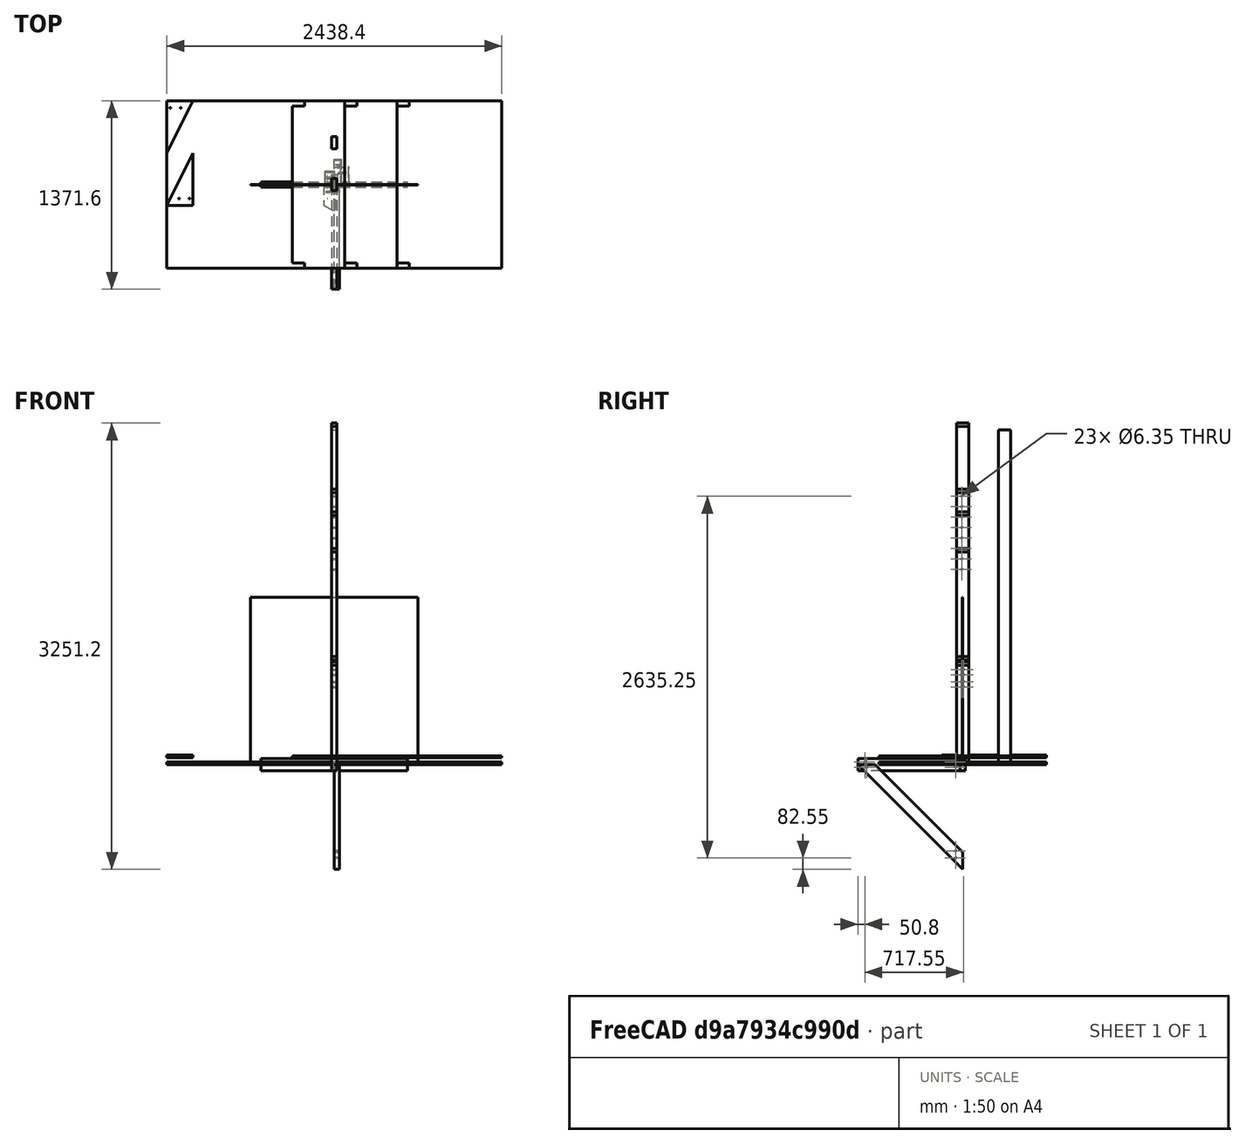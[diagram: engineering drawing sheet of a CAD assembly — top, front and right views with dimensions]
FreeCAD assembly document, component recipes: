
FREECAD ASSEMBLY — COMPONENT RECIPES ("workshop")

This assembly document has 20 components, labeled P0..P19 below (a component is one placed body or linked part). 20 of them carry a construction recipe — the FreeCAD feature program that regenerates the part from scratch, quoted from this document or its linked companion documents; the rest are supplied as boundary geometry only. No exploded tour is included for this assembly.
COMPONENT P0 — recipe-attached ("P_Electronics_CableMount", modeled in this document).
Construction recipe (the document's own serialized feature program — sketch geometry with constraints, then the solid features built on it; lengths are millimeters unless a unit is written):

FEATURE [Sketcher::SketchObject] Sketch  label="S_Electronics_CableMount_Body"
  FullyConstrained = true
  MapMode = 5
  Support = -> [XY_Plane001]
  sketch-geometry (8):
    g0: LineSegment StartX=12.5 StartY=42.5 StartZ=0 EndX=12.5 EndY=12.5 EndZ=0
    g1: LineSegment StartX=-12.5 StartY=12.5 StartZ=0 EndX=-12.5 EndY=42.5 EndZ=0
    g2: ArcOfCircle CenterX=3e-15 CenterY=12.5 CenterZ=0 NormalX=0 NormalY=0 NormalZ=1 AngleXU=0 Radius=12.5 StartAngle=3.14159 EndAngle=6.28319
    g3: LineSegment StartX=22.5 StartY=42.5 StartZ=0 EndX=22.5 EndY=12.5 EndZ=0
    g4: LineSegment StartX=-22.5 StartY=12.5 StartZ=0 EndX=-22.5 EndY=42.5 EndZ=0
    g5: ArcOfCircle CenterX=5.7957e-12 CenterY=12.5 CenterZ=0 NormalX=0 NormalY=0 NormalZ=1 AngleXU=0 Radius=22.5 StartAngle=3.14159 EndAngle=6.28319
    g6: LineSegment StartX=-12.5 StartY=42.5 StartZ=0 EndX=-22.5 EndY=42.5 EndZ=0
    g7: LineSegment StartX=22.5 StartY=42.5 StartZ=0 EndX=12.5 EndY=42.5 EndZ=0
  constraints (20):
    c: Vertical(g0)
    c: Symmetric(g0,g1,g-2)
    c: PointOnObject(g-1,g2)
    c: Tangent(g2,g0) = 1.5708
    c: Tangent(g1,g2) = 1.5708
    c: Vertical(g3)
    c: Coincident(g6,g1)
    c: Coincident(g6,g4)
    c: Coincident(g7,g3)
    c: Coincident(g7,g0)
    c: Tangent(g5,g3) = 1.5708
    c: Tangent(g4,g5) = 1.5708
    c: Horizontal(g6)
    c: Horizontal(g7)
    c: Horizontal(g4,g3)
    c: Horizontal(g4,g1)
    c: Symmetric(g3,g4,g-2)
    c: DistanceX(g7,g7) = 10
    c: DistanceX(g1,g0) = 25
    c: DistanceY(g3,g3) = 30
FEATURE [PartDesign::Pad] Pad  label="PAD_Electronics_CableMount"
  Direction = (0,0,1)
  Length = 10
  Length2 = 10
  Profile = -> Sketch
  ReferenceAxis = -> Sketch [N_Axis]
  Type = 0
FEATURE [Sketcher::SketchObject] Sketch001  label="S_Electronics_CableMount_Hole"
  AttachmentOffset = pos=(0,0,30) rot=(0,0,1;0rad)
  FullyConstrained = true
  MapMode = 5
  Placement = pos=(30,-6.7e-15,6.7e-15) rot=(0.57735,0.57735,0.57735;2.0944rad)
  Support = -> [YZ_Plane001]
  sketch-geometry (1):
    g0: Circle CenterX=35 CenterY=5 CenterZ=0 NormalX=0 NormalY=0 NormalZ=1 AngleXU=0 Radius=2.5
  constraints (3):
    c: Diameter(g0) = 5
    c: DistanceY(g-1,g0) = 5
    c: DistanceX(g-1,g0) = 35
FEATURE [PartDesign::Hole] Hole  label="HOLE_Electronics_CableMount"
  BaseFeature = -> Pad
  CustomThreadClearance = 0
  Depth = 161.858
  DepthType = 1
  Diameter = 5.5
  DrillForDepth = false
  DrillPoint = 0
  DrillPointAngle = 118
  HoleCutCountersinkAngle = 90
  HoleCutCustomValues = false
  HoleCutDepth = 0
  HoleCutDiameter = 6.1
  HoleCutType = 0
  ModelThread = false
  Profile = -> Sketch001
  Tapered = false
  TaperedAngle = 90
  ThreadClass = 0
  ThreadDepth = 161.858
  ThreadDepthType = 0
  ThreadDirection = 0
  ThreadFit = 0
  ThreadSize = 13
  ThreadType = 1
  Threaded = false
  UseCustomThreadClearance = false
FEATURE [PartDesign::Body] Body  label="B_Electronics_CableMount"
  Group = -> [Sketch,Pad,Sketch001,Hole]
  Origin = -> Origin001
  Tip = -> Hole
COMPONENT P1 — recipe-attached ("P_Electronics_CableMountSpacer", modeled in this document).
Construction recipe (the document's own serialized feature program — sketch geometry with constraints, then the solid features built on it; lengths are millimeters unless a unit is written):

FEATURE [Sketcher::SketchObject] Sketch002  label="S_Electronics_CableMountSpacer"
  FullyConstrained = true
  MapMode = 5
  Support = -> [XY_Plane003]
  sketch-geometry (7):
    g0: LineSegment StartX=-25 StartY=0 StartZ=0 EndX=25 EndY=0 EndZ=0
    g1: LineSegment StartX=25 StartY=0 StartZ=0 EndX=25 EndY=70 EndZ=0
    g2: LineSegment StartX=25 StartY=70 StartZ=0 EndX=-25 EndY=70 EndZ=0
    g3: LineSegment StartX=-25 StartY=70 StartZ=0 EndX=-25 EndY=0 EndZ=0
    g4: Circle CenterX=0 CenterY=60 CenterZ=0 NormalX=0 NormalY=0 NormalZ=1 AngleXU=0 Radius=2.5
    g5: Circle CenterX=0 CenterY=35 CenterZ=0 NormalX=0 NormalY=0 NormalZ=1 AngleXU=0 Radius=2.5
    g6: Circle CenterX=0 CenterY=10 CenterZ=0 NormalX=0 NormalY=0 NormalZ=1 AngleXU=0 Radius=2.5
  constraints (20):
    c: Coincident(g0,g1)
    c: Coincident(g1,g2)
    c: Coincident(g2,g3)
    c: Coincident(g3,g0)
    c: Horizontal(g2)
    c: Vertical(g1)
    c: Vertical(g3)
    c: PointOnObject(g0,g-1)
    c: Symmetric(g0,g0,g-2)
    c: DistanceX(g2,g2) = 50
    c: DistanceY(g1,g1) = 70
    c: PointOnObject(g4,g-2)
    c: PointOnObject(g5,g-2)
    c: PointOnObject(g6,g-2)
    c: Equal(g6,g5)
    c: Equal(g5,g4)
    c: Diameter(g4) = 5
    c: DistanceY(g-1,g6) = 10
    c: DistanceY(g4,g2) = 10
    c: DistanceY(g-1,g5) = 35
FEATURE [PartDesign::Pad] Pad001  label="PAD_Electronics_CableMountSpacer"
  Direction = (0,0,1)
  Length = 2
  Length2 = 10
  Profile = -> Sketch002
  ReferenceAxis = -> Sketch002 [N_Axis]
  Type = 0
FEATURE [Sketcher::SketchObject] Sketch003  label="S_Electronics_CableMountSpacer_Side"
  FullyConstrained = true
  MapMode = 5
  Support = -> [XY_Plane003]
  expr: Constraints[9] = 41.5 mm / 2
  sketch-geometry (4):
    g0: LineSegment StartX=20.75 StartY=70 StartZ=0 EndX=25 EndY=70 EndZ=0
    g1: LineSegment StartX=25 StartY=70 StartZ=0 EndX=25 EndY=0 EndZ=0
    g2: LineSegment StartX=25 StartY=0 StartZ=0 EndX=20.75 EndY=0 EndZ=0
    g3: LineSegment StartX=20.75 StartY=0 StartZ=0 EndX=20.75 EndY=70 EndZ=0
  constraints (12):
    c: Coincident(g0,g1)
    c: Coincident(g1,g2)
    c: Coincident(g2,g3)
    c: Coincident(g3,g0)
    c: Horizontal(g0)
    c: Horizontal(g2)
    c: Vertical(g1)
    c: Vertical(g3)
    c: PointOnObject(g1,g-1)
    c: DistanceX(g-1,g2) = 20.75
    c: DistanceX(g-1,g1) = 25
    c: DistanceY(g1,g1) = 70
FEATURE [PartDesign::Pad] Pad002  label="PAD_Electronics_CableMountSpacer_Side"
  BaseFeature = -> Pad001
  Direction = (0,0,1)
  Length = 4
  Length2 = 10
  Profile = -> Sketch003
  ReferenceAxis = -> Sketch003 [N_Axis]
  Type = 0
FEATURE [PartDesign::Mirrored] Mirrored  label="PAT_Electronics_CableMountSpacer_Side"
  BaseFeature = -> Pad002
  MirrorPlane = -> Sketch003 [V_Axis]
  Originals = -> [Pad002]
FEATURE [PartDesign::Body] Body001  label="B_Electronics_CableMountSpacer"
  Group = -> [Sketch002,Pad001,Sketch003,Pad002,Mirrored]
  Origin = -> Origin003
  Tip = -> Mirrored
COMPONENT P2 — recipe-attached ("P_Workbench_Top", modeled in this document).
Construction recipe (the document's own serialized feature program — sketch geometry with constraints, then the solid features built on it; lengths are millimeters unless a unit is written):

FEATURE [Sketcher::SketchObject] Sketch005  label="S_Workbench_Top_Base"
  FullyConstrained = true
  MapMode = 5
  Support = -> [XY_Plane007]
  expr: Constraints[8] = <<S_Workbench_Master>>.Constraints.TableWidth
  sketch-geometry (4):
    g0: LineSegment StartX=-609.6 StartY=0 StartZ=0 EndX=609.6 EndY=0 EndZ=0
    g1: LineSegment StartX=609.6 StartY=0 StartZ=0 EndX=609.6 EndY=-762 EndZ=0
    g2: LineSegment StartX=609.6 StartY=-762 StartZ=0 EndX=-609.6 EndY=-762 EndZ=0
    g3: LineSegment StartX=-609.6 StartY=-762 StartZ=0 EndX=-609.6 EndY=0 EndZ=0
  constraints (11):
    c: Coincident(g0,g1)
    c: Coincident(g1,g2)
    c: Coincident(g2,g3)
    c: Coincident(g3,g0)
    c: Horizontal(g0)
    c: Horizontal(g2)
    c: Vertical(g1)
    c: Vertical(g3)
    c: DistanceX(g0,g0) = 1219.2
    c: DistanceY(g1,g1) = 762
    c: Symmetric(g0,g0,g-1)
FEATURE [PartDesign::Pad] Pad004  label="PAD_Workbench_Top_Base"
  Direction = (0,0,1)
  Length = 12.7
  Length2 = 10
  Profile = -> Sketch005
  ReferenceAxis = -> Sketch005 [N_Axis]
  Type = 0
  expr: Length = <<S_Workbench_Master>>.Constraints.TableThickness
FEATURE [Sketcher::SketchObject] Sketch006  label="S_Workbench_Top_BackHole"
  ExternalGeometry = -> [Pad004]
  FullyConstrained = true
  MapMode = 5
  Placement = pos=(0,0,12.7) rot=(0,0,1;0rad)
  Support = -> [Pad004]
  expr: Constraints[8] = Sketch009.Constraints.TwobyfourWidth
  expr: Constraints[9] = Sketch009.Constraints.TwobyfourHeight
  sketch-geometry (4):
    g0: LineSegment StartX=-571.5 StartY=0 StartZ=0 EndX=-609.6 EndY=0 EndZ=0
    g1: LineSegment StartX=-609.6 StartY=0 StartZ=0 EndX=-609.6 EndY=-88.9 EndZ=0
    g2: LineSegment StartX=-609.6 StartY=-88.9 StartZ=0 EndX=-571.5 EndY=-88.9 EndZ=0
    g3: LineSegment StartX=-571.5 StartY=-88.9 StartZ=0 EndX=-571.5 EndY=0 EndZ=0
  constraints (11):
    c: Coincident(g0,g1)
    c: Coincident(g1,g2)
    c: Coincident(g2,g3)
    c: Coincident(g3,g0)
    c: Horizontal(g0)
    c: Horizontal(g2)
    c: Vertical(g1)
    c: Vertical(g3)
    c: DistanceX(g0,g0) = 38.1
    c: DistanceY(g3,g3) = 88.9
    c: Coincident(g0,g-3)
FEATURE [PartDesign::Pocket] Pocket  label="POCKET_Workbench_Top_BackHole"
  BaseFeature = -> Pad004
  Direction = (0,0,-1)
  Length = 25.4
  Length2 = 5
  Profile = -> Sketch006
  ReferenceAxis = -> Sketch006 [N_Axis]
  Type = 0
FEATURE [PartDesign::Mirrored] Mirrored001  label="PAT_B_Workbench_Top_BackHoles"
  BaseFeature = -> Pocket
  MirrorPlane = -> Sketch006 [V_Axis]
  Originals = -> [Pocket]
FEATURE [PartDesign::Body] Body003  label="B_Workbench_Top"
  Group = -> [Sketch005,Pad004,Sketch006,Pocket,Mirrored001]
  Origin = -> Origin007
  Tip = -> Mirrored001
COMPONENT P3 — recipe-attached ("P_Workbench_BackLeg", modeled in this document).
Construction recipe (the document's own serialized feature program — sketch geometry with constraints, then the solid features built on it; lengths are millimeters unless a unit is written):

FEATURE [Sketcher::SketchObject] Sketch007  label="S_Workbench_BackLeg_Base"
  FullyConstrained = true
  MapMode = 5
  Support = -> [XY_Plane010]
  expr: Constraints[10] = Sketch009.Constraints.TwobyfourHeight
  expr: Constraints[9] = Sketch009.Constraints.TwobyfourWidth
  sketch-geometry (4):
    g0: LineSegment StartX=-19.05 StartY=44.45 StartZ=0 EndX=19.05 EndY=44.45 EndZ=0
    g1: LineSegment StartX=19.05 StartY=44.45 StartZ=0 EndX=19.05 EndY=-44.45 EndZ=0
    g2: LineSegment StartX=19.05 StartY=-44.45 StartZ=0 EndX=-19.05 EndY=-44.45 EndZ=0
    g3: LineSegment StartX=-19.05 StartY=-44.45 StartZ=0 EndX=-19.05 EndY=44.45 EndZ=0
  constraints (11):
    c: Coincident(g0,g1)
    c: Coincident(g1,g2)
    c: Coincident(g2,g3)
    c: Coincident(g3,g0)
    c: Horizontal(g0)
    c: Horizontal(g2)
    c: Vertical(g1)
    c: Vertical(g3)
    c: Symmetric(g0,g1,g-1)
    c: DistanceX(g0,g0) = 38.1
    c: DistanceY(g1,g1) = 88.9
FEATURE [PartDesign::Pad] Pad005  label="PAD_Workbench_BackLeg"
  Direction = (0,0,1)
  Length = 1981.2
  Length2 = 10
  Profile = -> Sketch007
  ReferenceAxis = -> Sketch007 [N_Axis]
  Type = 0
  expr: Length = <<S_Workbench_Master>>.Constraints.BackLegHeight
FEATURE [Sketcher::SketchObject] Sketch019  label="S_Workbench_BackLeg_Holes"
  FullyConstrained = true
  MapMode = 5
  Placement = pos=(0,0,0) rot=(0.57735,0.57735,0.57735;2.0944rad)
  Support = -> [YZ_Plane010]
  expr: Constraints[15] = <<S_Workbench_Master>>.Constraints.ShelfHeight - 1 in
  expr: Constraints[16] = <<S_Workbench_Master>>.Constraints.ShelfHeight + <<S_Workbench_Master>>.Constraints.ShelfSpacing - 1 in
  expr: Constraints[22] = Sketch009.Constraints.TwobyfourHeight - 2 in
  expr: Constraints[23] = Sketch009.Constraints.TwobyfourHeight
  expr: Constraints[25] = <<S_Workbench_Master>>.Constraints.BackLegHeight
  expr: Constraints[2] = Sketch009.Constraints.BoltDiameter
  expr: Constraints[3] = <<S_Workbench_Master>>.Constraints.TableHeight - 1.75 in
  expr: Constraints[4] = Sketch009.Constraints.TwobyfourHeight - 2 in
  sketch-geometry (13):
    g0: Circle CenterX=-6.35 CenterY=692.15 CenterZ=0 NormalX=0 NormalY=0 NormalZ=1 AngleXU=0 Radius=3.175
    g1: Circle CenterX=-6.35 CenterY=654.05 CenterZ=0 NormalX=0 NormalY=0 NormalZ=1 AngleXU=0 Radius=3.175
    g2: Circle CenterX=-6.35 CenterY=1498.6 CenterZ=0 NormalX=0 NormalY=0 NormalZ=1 AngleXU=0 Radius=3.175
    g3: Circle CenterX=-6.35 CenterY=1422.4 CenterZ=0 NormalX=0 NormalY=0 NormalZ=1 AngleXU=0 Radius=3.175
    g4: Circle CenterX=-6.35 CenterY=1803.4 CenterZ=0 NormalX=0 NormalY=0 NormalZ=1 AngleXU=0 Radius=3.175
    g5: Circle CenterX=-6.35 CenterY=1727.2 CenterZ=0 NormalX=0 NormalY=0 NormalZ=1 AngleXU=0 Radius=3.175
    g6: Circle CenterX=-6.35 CenterY=603.25 CenterZ=0 NormalX=0 NormalY=0 NormalZ=1 AngleXU=0 Radius=3.175
    g7: Circle CenterX=-6.35 CenterY=565.15 CenterZ=0 NormalX=0 NormalY=0 NormalZ=1 AngleXU=0 Radius=3.175
    g8: GeomPoint X=0 Y=1981.2 Z=0
    g9: Circle CenterX=-6.35 CenterY=1879.6 CenterZ=0 NormalX=0 NormalY=0 NormalZ=1 AngleXU=0 Radius=3.175
    g10: Circle CenterX=-6.35 CenterY=1955.8 CenterZ=0 NormalX=0 NormalY=0 NormalZ=1 AngleXU=0 Radius=3.175
    g11: Circle CenterX=-6.35 CenterY=1651 CenterZ=0 NormalX=0 NormalY=0 NormalZ=1 AngleXU=0 Radius=3.175
    g12: Circle CenterX=-6.35 CenterY=1574.8 CenterZ=0 NormalX=0 NormalY=0 NormalZ=1 AngleXU=0 Radius=3.175
  constraints (41):
    c: Vertical(g1,g0)
    c: Equal(g0,g1)
    c: Diameter(g0) = 6.35
    c: DistanceY(g-1,g0) = 692.15
    c: DistanceY(g1,g0) = 38.1
    c: DistanceX(g0,g-1) = 6.35
    c: Vertical(g4,g5)
    c: Vertical(g5,g2)
    c: Vertical(g2,g3)
    c: Equal(g4,g5)
    c: Equal(g5,g2)
    c: Equal(g2,g3)
    c: Equal(g3,g0)
    c: DistanceY(g3,g2) = 76.2
    c: DistanceY(g5,g4) = 76.2
    c: DistanceY(g-1,g2) = 1498.6
    c: DistanceY(g-1,g4) = 1803.4
    c: Vertical(g0,g3)
    c: Equal(g7,g6)
    c: Vertical(g6,g7)
    c: Vertical(g7,g1)
    c: Equal(g7,g1)
    c: DistanceY(g7,g6) = 38.1
    c: DistanceY(g6,g0) = 88.9
    c: PointOnObject(g8,g-2)
    c: DistanceY(g-1,g8) = 1981.2
    c: DistanceY(g4,g8) = 177.8
    c: Vertical(g9,g10)
    c: Vertical(g10,g4)
    c: Equal(g9,g10)
    c: Equal(g10,g4)
    c: DistanceY(g4,g9) = 76.2
    c: DistanceY(g9,g10) = 76.2
    c: DistanceY(g10,g8) = 25.4
    c: Equal(g11,g12)
    c: Vertical(g5,g11)
    c: Vertical(g11,g12)
    c: DistanceY(g11,g5) = 76.2
    c: DistanceY(g12,g11) = 76.2
    c: DistanceY(g2,g12) = 76.2
    c: Equal(g11,g5)
FEATURE [PartDesign::Pocket] Pocket004  label="POCKET_Workbench_BackLeg_Holes"
  BaseFeature = -> Pad005
  Direction = (-1,2e-16,-3e-16)
  Length = 76.2
  Length2 = 5
  Midplane = true
  Profile = -> Sketch019
  ReferenceAxis = -> Sketch019 [N_Axis]
  Type = 0
  expr: Length = Sketch009.Constraints.TwobyfourWidth * 2
FEATURE [PartDesign::Body] Body004  label="B_Workbench_BackLeg"
  Group = -> [Sketch007,Pad005,Sketch019,Pocket004]
  Origin = -> Origin010
  Tip = -> Pocket004
COMPONENT P4 — recipe-attached ("P_Workbench_FrontLeg", modeled in this document).
Construction recipe (the document's own serialized feature program — sketch geometry with constraints, then the solid features built on it; lengths are millimeters unless a unit is written):

FEATURE [Sketcher::SketchObject] Sketch008  label="S_Workbench_FrontLeg_Base"
  FullyConstrained = true
  MapMode = 5
  Support = -> [XY_Plane012]
  expr: Constraints[10] = Sketch009.Constraints.TwobyfourHeight
  expr: Constraints[9] = Sketch009.Constraints.TwobyfourWidth
  sketch-geometry (4):
    g0: LineSegment StartX=-19.05 StartY=44.45 StartZ=0 EndX=19.05 EndY=44.45 EndZ=0
    g1: LineSegment StartX=19.05 StartY=44.45 StartZ=0 EndX=19.05 EndY=-44.45 EndZ=0
    g2: LineSegment StartX=19.05 StartY=-44.45 StartZ=0 EndX=-19.05 EndY=-44.45 EndZ=0
    g3: LineSegment StartX=-19.05 StartY=-44.45 StartZ=0 EndX=-19.05 EndY=44.45 EndZ=0
  constraints (11):
    c: Coincident(g0,g1)
    c: Coincident(g1,g2)
    c: Coincident(g2,g3)
    c: Coincident(g3,g0)
    c: Horizontal(g0)
    c: Horizontal(g2)
    c: Vertical(g1)
    c: Vertical(g3)
    c: Symmetric(g0,g1,g-1)
    c: DistanceX(g0,g0) = 38.1
    c: DistanceY(g1,g1) = 88.9
FEATURE [PartDesign::Pad] Pad006  label="PAD_Workbench_FrontLeg_Base"
  Direction = (0,0,1)
  Length = 723.9
  Length2 = 10
  Profile = -> Sketch008
  ReferenceAxis = -> Sketch008 [N_Axis]
  Type = 0
  expr: Length = Sketch009.Constraints.FrontLegHeight
FEATURE [Sketcher::SketchObject] Sketch018  label="S_Workbench_FrontLeg_Holes"
  FullyConstrained = true
  MapMode = 5
  Placement = pos=(0,0,0) rot=(0.57735,0.57735,0.57735;2.0944rad)
  Support = -> [YZ_Plane012]
  expr: Constraints[10] = Sketch009.Constraints.TwobyfourHeight - 2 in
  expr: Constraints[11] = Sketch009.Constraints.TwobyfourHeight
  expr: Constraints[1] = Sketch009.Constraints.BoltDiameter
  expr: Constraints[2] = Sketch009.Constraints.TwobyfourHeight - 2 in
  expr: Constraints[4] = <<S_Workbench_Master>>.Constraints.TableHeight - 1.75 in
  sketch-geometry (4):
    g0: Circle CenterX=6.35 CenterY=692.15 CenterZ=0 NormalX=0 NormalY=0 NormalZ=1 AngleXU=0 Radius=3.175
    g1: Circle CenterX=6.35 CenterY=654.05 CenterZ=0 NormalX=0 NormalY=0 NormalZ=1 AngleXU=0 Radius=3.175
    g2: Circle CenterX=6.35 CenterY=603.25 CenterZ=0 NormalX=0 NormalY=0 NormalZ=1 AngleXU=0 Radius=3.175
    g3: Circle CenterX=6.35 CenterY=565.15 CenterZ=0 NormalX=0 NormalY=0 NormalZ=1 AngleXU=0 Radius=3.175
  constraints (12):
    c: Equal(g0,g1)
    c: Diameter(g1) = 6.35
    c: DistanceY(g1,g0) = 38.1
    c: Vertical(g0,g1)
    c: DistanceY(g-1,g0) = 692.15
    c: DistanceX(g-1,g1) = 6.35
    c: Equal(g2,g1)
    c: Vertical(g3,g2)
    c: Vertical(g2,g1)
    c: Equal(g3,g2)
    c: DistanceY(g3,g2) = 38.1
    c: DistanceY(g2,g0) = 88.9
FEATURE [PartDesign::Pocket] Pocket003  label="POCKET_Workbench_FrontLeg_Holes"
  BaseFeature = -> Pad006
  Direction = (-1,2e-16,-3e-16)
  Length = 76.2
  Length2 = 5
  Midplane = true
  Profile = -> Sketch018
  ReferenceAxis = -> Sketch018 [N_Axis]
  Type = 0
  expr: Length = Sketch009.Constraints.TwobyfourWidth * 2
FEATURE [PartDesign::Body] Body005  label="B_Workbench_FrontLeg"
  Group = -> [Sketch008,Pad006,Sketch018,Pocket003]
  Origin = -> Origin012
  Tip = -> Pocket003
COMPONENT P5 — recipe-attached ("P_Workbench_Shelf", modeled in this document).
Construction recipe (the document's own serialized feature program — sketch geometry with constraints, then the solid features built on it; lengths are millimeters unless a unit is written):

FEATURE [Sketcher::SketchObject] Sketch010  label="S_Workbench_Shelf_Base"
  FullyConstrained = true
  MapMode = 5
  Support = -> [XY_Plane014]
  expr: Constraints[10] = <<S_Workbench_Master>>.Constraints.ShelfDepth
  expr: Constraints[9] = <<S_Workbench_Master>>.Constraints.TableWidth
  sketch-geometry (4):
    g0: LineSegment StartX=-609.6 StartY=0 StartZ=0 EndX=609.6 EndY=0 EndZ=0
    g1: LineSegment StartX=609.6 StartY=0 StartZ=0 EndX=609.6 EndY=-381 EndZ=0
    g2: LineSegment StartX=609.6 StartY=-381 StartZ=0 EndX=-609.6 EndY=-381 EndZ=0
    g3: LineSegment StartX=-609.6 StartY=-381 StartZ=0 EndX=-609.6 EndY=0 EndZ=0
  constraints (11):
    c: Coincident(g0,g1)
    c: Coincident(g1,g2)
    c: Coincident(g2,g3)
    c: Coincident(g3,g0)
    c: Horizontal(g0)
    c: Horizontal(g2)
    c: Vertical(g1)
    c: Vertical(g3)
    c: Symmetric(g0,g0,g-1)
    c: DistanceX(g0,g0) = 1219.2
    c: DistanceY(g1,g1) = 381
FEATURE [PartDesign::Pad] Pad007  label="PAD_Workbench_Shelf_Base"
  Direction = (0,0,1)
  Length = 12.7
  Length2 = 10
  Profile = -> Sketch010
  ReferenceAxis = -> Sketch010 [N_Axis]
  Type = 0
  expr: Length = <<S_Workbench_Master>>.Constraints.TableThickness
FEATURE [Sketcher::SketchObject] Sketch011  label="S_Workbench_Shelf_LegSlot"
  FullyConstrained = true
  MapMode = 5
  Support = -> [XY_Plane014]
  expr: Constraints[10] = Sketch009.Constraints.TwobyfourWidth
  expr: Constraints[11] = <<S_Workbench_Master>>.Constraints.TableWidth / 2
  expr: Constraints[9] = Sketch009.Constraints.TwobyfourHeight
  sketch-geometry (4):
    g0: LineSegment StartX=-609.6 StartY=0 StartZ=0 EndX=-571.5 EndY=0 EndZ=0
    g1: LineSegment StartX=-571.5 StartY=0 StartZ=0 EndX=-571.5 EndY=-88.9 EndZ=0
    g2: LineSegment StartX=-571.5 StartY=-88.9 StartZ=0 EndX=-609.6 EndY=-88.9 EndZ=0
    g3: LineSegment StartX=-609.6 StartY=-88.9 StartZ=0 EndX=-609.6 EndY=0 EndZ=0
  constraints (12):
    c: Coincident(g0,g1)
    c: Coincident(g1,g2)
    c: Coincident(g2,g3)
    c: Coincident(g3,g0)
    c: Horizontal(g0)
    c: Horizontal(g2)
    c: Vertical(g1)
    c: Vertical(g3)
    c: Horizontal(g0,g-1)
    c: DistanceY(g1,g1) = 88.9
    c: DistanceX(g2,g2) = 38.1
    c: DistanceX(g0,g-1) = 609.6
FEATURE [PartDesign::Pocket] Pocket001  label="POCKET_Workbench_Shelf_LegSlot"
  BaseFeature = -> Pad007
  Direction = (0,0,-1)
  Length = 25.4
  Length2 = 5
  Profile = -> Sketch011
  ReferenceAxis = -> Sketch011 [N_Axis]
  Reversed = true
  Type = 0
  expr: Length = <<S_Workbench_Master>>.Constraints.TableThickness * 2
FEATURE [PartDesign::Mirrored] Mirrored002  label="PAT_Workbench_Shelf_LegSlots"
  BaseFeature = -> Pocket001
  MirrorPlane = -> Sketch011 [V_Axis]
  Originals = -> [Pocket001]
FEATURE [PartDesign::Body] Body006  label="B_Workbench_Shelf"
  Group = -> [Sketch010,Pad007,Sketch011,Pocket001,Mirrored002]
  Origin = -> Origin014
  Tip = -> Mirrored002
COMPONENT P6 — recipe-attached ("P_Workbench_SideBrace", modeled in this document).
Construction recipe (the document's own serialized feature program — sketch geometry with constraints, then the solid features built on it; lengths are millimeters unless a unit is written):

FEATURE [Sketcher::SketchObject] Sketch012  label="S_Workbench_SideBrace_Body"
  FullyConstrained = true
  MapMode = 5
  Placement = pos=(0,0,0) rot=(1,0,0;1.5708rad)
  Support = -> [XZ_Plane016]
  expr: Constraints[10] = Sketch009.Constraints.TwobyfourHeight
  expr: Constraints[9] = Sketch009.Constraints.TwobyfourWidth
  sketch-geometry (4):
    g0: LineSegment StartX=-19.05 StartY=44.45 StartZ=0 EndX=19.05 EndY=44.45 EndZ=0
    g1: LineSegment StartX=19.05 StartY=44.45 StartZ=0 EndX=19.05 EndY=-44.45 EndZ=0
    g2: LineSegment StartX=19.05 StartY=-44.45 StartZ=0 EndX=-19.05 EndY=-44.45 EndZ=0
    g3: LineSegment StartX=-19.05 StartY=-44.45 StartZ=0 EndX=-19.05 EndY=44.45 EndZ=0
  constraints (11):
    c: Coincident(g0,g1)
    c: Coincident(g1,g2)
    c: Coincident(g2,g3)
    c: Coincident(g3,g0)
    c: Horizontal(g0)
    c: Horizontal(g2)
    c: Vertical(g1)
    c: Vertical(g3)
    c: Symmetric(g0,g1,g-1)
    c: DistanceX(g0,g0) = 38.1
    c: DistanceY(g1,g1) = 88.9
FEATURE [PartDesign::Pad] Pad008  label="PAD_Workbench_SideBrace_Body"
  Direction = (0,-1,-2e-16)
  Length = 762
  Length2 = 10
  Placement = pos=(0,0,0) rot=(1,0,0;1.5708rad)
  Profile = -> Sketch012
  ReferenceAxis = -> Sketch012 [N_Axis]
  Type = 0
  expr: Length = <<S_Workbench_Master>>.Constraints.TableDepth
FEATURE [Sketcher::SketchObject] Sketch017  label="S_Workbench_SideBrace_Holes"
  FullyConstrained = true
  MapMode = 5
  Placement = pos=(0,0,0) rot=(0.57735,0.57735,0.57735;2.0944rad)
  Support = -> [YZ_Plane016]
  expr: Constraints[17] = Sketch009.Constraints.TwobyfourHeight - 2 in
  expr: Constraints[18] = <<S_Workbench_Master>>.Constraints.TableDepth - 2 in
  expr: Constraints[7] = Sketch009.Constraints.BoltDiameter
  sketch-geometry (8):
    g0: Circle CenterX=-50.8 CenterY=19.05 CenterZ=0 NormalX=0 NormalY=0 NormalZ=1 AngleXU=0 Radius=3.175
    g1: Circle CenterX=-50.8 CenterY=-19.05 CenterZ=0 NormalX=0 NormalY=0 NormalZ=1 AngleXU=0 Radius=3.175
    g2: Circle CenterX=-711.2 CenterY=19.05 CenterZ=0 NormalX=0 NormalY=0 NormalZ=1 AngleXU=0 Radius=3.175
    g3: Circle CenterX=-711.2 CenterY=-19.05 CenterZ=0 NormalX=0 NormalY=0 NormalZ=1 AngleXU=0 Radius=3.175
    g4: LineSegment StartX=-711.2 StartY=-19.05 StartZ=0 EndX=-711.2 EndY=0 EndZ=0
    g5: LineSegment StartX=-711.2 StartY=0 StartZ=0 EndX=-711.2 EndY=19.05 EndZ=0
    g6: LineSegment StartX=-50.8 StartY=-19.05 StartZ=0 EndX=-50.8 EndY=0 EndZ=0
    g7: LineSegment StartX=-50.8 StartY=0 StartZ=0 EndX=-50.8 EndY=19.05 EndZ=0
  constraints (20):
    c: Coincident(g4,g3)
    c: PointOnObject(g4,g-1)
    c: Coincident(g5,g2)
    c: Tangent(g5,g4) = -1.5708
    c: Equal(g5,g4)
    c: Equal(g2,g3)
    c: Equal(g0,g1)
    c: Diameter(g0) = 6.35
    c: Coincident(g6,g1)
    c: PointOnObject(g6,g-1)
    c: Coincident(g0,g7)
    c: Tangent(g6,g7) = -1.5708
    c: Equal(g7,g6)
    c: Equal(g5,g7)
    c: DistanceX(g6,g-1) = 50.8
    c: Vertical(g5)
    c: Vertical(g7)
    c: DistanceY(g1,g0) = 38.1
    c: DistanceX(g4,g-1) = 711.2
    c: Equal(g3,g0)
FEATURE [PartDesign::Pocket] Pocket002  label="POCKET_Workbench_SideBrace_Holes"
  BaseFeature = -> Pad008
  Direction = (-1,2e-16,-3e-16)
  Length = 50.8
  Length2 = 5
  Midplane = true
  Placement = pos=(0,0,0) rot=(1,0,0;1.5708rad)
  Profile = -> Sketch017
  ReferenceAxis = -> Sketch017 [N_Axis]
  Type = 0
FEATURE [PartDesign::Body] Body007  label="B_Workbench_SideBrace"
  Group = -> [Sketch012,Pad008,Sketch017,Pocket002]
  Origin = -> Origin016
  Tip = -> Pocket002
COMPONENT P7 — recipe-attached ("P_Workbench_Back", modeled in this document).
Construction recipe (the document's own serialized feature program — sketch geometry with constraints, then the solid features built on it; lengths are millimeters unless a unit is written):

FEATURE [Sketcher::SketchObject] Sketch013  label="S_Workbench_Back_Base"
  FullyConstrained = true
  MapMode = 5
  Placement = pos=(0,0,0) rot=(1,0,0;1.5708rad)
  Support = -> [XZ_Plane018]
  expr: Constraints[10] = <<S_Workbench_Master>>.Constraints.BackHeight
  expr: Constraints[8] = <<S_Workbench_Master>>.Constraints.TableWidth
  sketch-geometry (4):
    g0: LineSegment StartX=-609.6 StartY=1219.2 StartZ=0 EndX=609.6 EndY=1219.2 EndZ=0
    g1: LineSegment StartX=609.6 StartY=1219.2 StartZ=0 EndX=609.6 EndY=0 EndZ=0
    g2: LineSegment StartX=609.6 StartY=0 StartZ=0 EndX=-609.6 EndY=0 EndZ=0
    g3: LineSegment StartX=-609.6 StartY=0 StartZ=0 EndX=-609.6 EndY=1219.2 EndZ=0
  constraints (11):
    c: Coincident(g0,g1)
    c: Coincident(g1,g2)
    c: Coincident(g2,g3)
    c: Coincident(g3,g0)
    c: Horizontal(g0)
    c: Horizontal(g2)
    c: Vertical(g1)
    c: Vertical(g3)
    c: DistanceX(g2,g2) = 1219.2
    c: Symmetric(g2,g1,g-1)
    c: DistanceY(g1,g1) = 1219.2
FEATURE [PartDesign::Pad] Pad009  label="PAD_Workbench_Back_Base"
  Direction = (0,-1,-2e-16)
  Length = 3.175
  Length2 = 10
  Placement = pos=(0,0,0) rot=(1,0,0;1.5708rad)
  Profile = -> Sketch013
  ReferenceAxis = -> Sketch013 [N_Axis]
  Type = 0
  expr: Length = <<S_Workbench_Master>>.Constraints.BackThickness
FEATURE [PartDesign::Body] Body008  label="B_Workbench_Back"
  Group = -> [Sketch013,Pad009]
  Origin = -> Origin018
  Tip = -> Pad009
COMPONENT P8 — recipe-attached ("P_Workbench_BackBrace", modeled in this document).
Construction recipe (the document's own serialized feature program — sketch geometry with constraints, then the solid features built on it; lengths are millimeters unless a unit is written):

FEATURE [Sketcher::SketchObject] Sketch014  label="S_Workbench_BackBrace_Body"
  FullyConstrained = true
  MapMode = 5
  Placement = pos=(0,0,0) rot=(0.57735,0.57735,0.57735;2.0944rad)
  Support = -> [YZ_Plane020]
  expr: Constraints[10] = Sketch009.Constraints.TwobyfourHeight
  expr: Constraints[9] = Sketch009.Constraints.TwobyfourWidth
  sketch-geometry (4):
    g0: LineSegment StartX=-19.05 StartY=44.45 StartZ=0 EndX=19.05 EndY=44.45 EndZ=0
    g1: LineSegment StartX=19.05 StartY=44.45 StartZ=0 EndX=19.05 EndY=-44.45 EndZ=0
    g2: LineSegment StartX=19.05 StartY=-44.45 StartZ=0 EndX=-19.05 EndY=-44.45 EndZ=0
    g3: LineSegment StartX=-19.05 StartY=-44.45 StartZ=0 EndX=-19.05 EndY=44.45 EndZ=0
  constraints (11):
    c: Coincident(g0,g1)
    c: Coincident(g1,g2)
    c: Coincident(g2,g3)
    c: Coincident(g3,g0)
    c: Horizontal(g0)
    c: Horizontal(g2)
    c: Vertical(g1)
    c: Vertical(g3)
    c: Symmetric(g0,g1,g-1)
    c: DistanceX(g0,g0) = 38.1
    c: DistanceY(g1,g1) = 88.9
FEATURE [PartDesign::Pad] Pad010  label="PAD_Workbench_BackBrace_Body"
  Direction = (1,-2e-16,3e-16)
  Length = 1066.8
  Length2 = 10
  Midplane = true
  Placement = pos=(0,0,0) rot=(1,1,1;2.0944rad)
  Profile = -> Sketch014
  ReferenceAxis = -> Sketch014 [N_Axis]
  Type = 0
  expr: Length = <<S_Workbench_Master>>.Constraints.TableWidth - 4 * Sketch009.Constraints.TwobyfourWidth
FEATURE [PartDesign::Body] Body009  label="B_Workbench_BackBrace"
  Group = -> [Sketch014,Pad010]
  Origin = -> Origin020
  Tip = -> Pad010
COMPONENT P9 — recipe-attached ("P_Workbench_ShelfBrace", modeled in this document).
Construction recipe (the document's own serialized feature program — sketch geometry with constraints, then the solid features built on it; lengths are millimeters unless a unit is written):

FEATURE [Sketcher::SketchObject] Sketch015  label="S_Workbench_ShelfBrace_Base"
  FullyConstrained = true
  MapMode = 5
  Placement = pos=(0,0,0) rot=(0.57735,0.57735,0.57735;2.0944rad)
  Support = -> [YZ_Plane022]
  expr: Constraints[6] = <<S_Workbench_Master>>.Constraints.ShelfDepth
  expr: Constraints[7] = <<S_Workbench_Master>>.Constraints.ShelfDepth / 2
  sketch-geometry (3):
    g0: LineSegment StartX=0 StartY=0 StartZ=0 EndX=0 EndY=-190.5 EndZ=0
    g1: LineSegment StartX=0 StartY=0 StartZ=0 EndX=-381 EndY=0 EndZ=0
    g2: LineSegment StartX=-381 StartY=0 StartZ=0 EndX=0 EndY=-190.5 EndZ=0
  constraints (8):
    c: Coincident(g0,g-1)
    c: PointOnObject(g0,g-2)
    c: Coincident(g1,g0)
    c: PointOnObject(g1,g-1)
    c: Coincident(g2,g1)
    c: Coincident(g2,g0)
    c: DistanceX(g1,g1) = 381
    c: DistanceY(g0,g0) = 190.5
FEATURE [PartDesign::Pad] Pad011  label="PAD_Workbench_ShelfBrace_Base"
  Direction = (1,-2e-16,3e-16)
  Length = 19.05
  Length2 = 10
  Placement = pos=(0,0,0) rot=(1,1,1;2.0944rad)
  Profile = -> Sketch015
  ReferenceAxis = -> Sketch015 [N_Axis]
  Type = 0
FEATURE [Sketcher::SketchObject] Sketch020  label="S_Workbench_ShelfBrace_Holes"
  FullyConstrained = true
  MapMode = 5
  Placement = pos=(0,0,0) rot=(0.57735,0.57735,0.57735;2.0944rad)
  Support = -> [YZ_Plane022]
  expr: Constraints[2] = <<S_Workbench_Master>>.Constraints.BoltDiameter
  expr: Constraints[3] = <<S_Workbench_Master>>.Constraints.TwobyfourHeight / 2 + 0.25 in
  sketch-geometry (2):
    g0: Circle CenterX=-50.8 CenterY=-25.4 CenterZ=0 NormalX=0 NormalY=0 NormalZ=1 AngleXU=0 Radius=3.175
    g1: Circle CenterX=-50.8 CenterY=-101.6 CenterZ=0 NormalX=0 NormalY=0 NormalZ=1 AngleXU=0 Radius=3.175
  constraints (6):
    c: Equal(g0,g1)
    c: Vertical(g0,g1)
    c: Diameter(g0) = 6.35
    c: DistanceX(g0,g-1) = 50.8
    c: DistanceY(g1,g0) = 76.2
    c: DistanceY(g0,g-1) = 25.4
FEATURE [PartDesign::Pocket] Pocket005  label="POCKET_Workbench_ShelfBrace_Holes"
  BaseFeature = -> Pad011
  Direction = (-1,2e-16,-3e-16)
  Length = 76.2
  Length2 = 5
  Placement = pos=(0,0,0) rot=(1,1,1;2.0944rad)
  Profile = -> Sketch020
  ReferenceAxis = -> Sketch020 [N_Axis]
  Reversed = true
  Type = 0
FEATURE [PartDesign::Body] Body010  label="B_Workbench_ShelfBrace"
  Group = -> [Sketch015,Pad011,Sketch020,Pocket005]
  Origin = -> Origin022
  Tip = -> Pocket005
COMPONENT P10 — recipe-attached ("P_Workbench_AngleBrace", modeled in this document).
Construction recipe (the document's own serialized feature program — sketch geometry with constraints, then the solid features built on it; lengths are millimeters unless a unit is written):

FEATURE [Sketcher::SketchObject] Sketch016  label="S_Workbench_AngleBrace_Base"
  FullyConstrained = false
  MapMode = 5
  Placement = pos=(0,0,0) rot=(0.57735,0.57735,0.57735;2.0944rad)
  Support = -> [YZ_Plane024]
  expr: Constraints[10] = <<S_Workbench_Master>>.Constraints.TableDepth
  sketch-geometry (5):
    g0: LineSegment StartX=-636.276 StartY=0 StartZ=0 EndX=0 EndY=-636.276 EndZ=0
    g1: LineSegment StartX=-762 StartY=0 StartZ=0 EndX=0 EndY=-762 EndZ=0
    g2: LineSegment StartX=-253.382 StartY=-382.895 StartZ=0 EndX=-316.243 EndY=-445.757 EndZ=0
    g3: LineSegment StartX=-762 StartY=0 StartZ=0 EndX=-636.276 EndY=0 EndZ=0
    g4: LineSegment StartX=0 StartY=-636.276 StartZ=0 EndX=0 EndY=-762 EndZ=0
  constraints (17):
    c: Vertical(g0,g-1)
    c: PointOnObject(g1,g-1)
    c: PointOnObject(g1,g-2)
    c: Parallel(g1,g0)
    c: Angle(g-2,g1) = 0.785398
    c: PointOnObject(g0,g-1)
    c: PointOnObject(g2,g0)
    c: PointOnObject(g2,g1)
    c: Perpendicular(g0,g2)
    c: Distance(g2) = 88.9
    c: DistanceX(g1,g-1) = 762
    c: Distance(g1) = 1077.63  'SideBraceLength'
    c: Coincident(g3,g1)
    c: Coincident(g3,g0)
    c: Coincident(g4,g0)
    c: Coincident(g4,g1)
    c: DistanceY(g1,g-1) = 762
FEATURE [PartDesign::Pad] Pad012  label="PAD_Workbench_AngleBrace_Base"
  Direction = (1,-2e-16,3e-16)
  Length = 38.1
  Length2 = 10
  Placement = pos=(0,0,0) rot=(1,1,1;2.0944rad)
  Profile = -> Sketch016
  ReferenceAxis = -> Sketch016 [N_Axis]
  Type = 0
FEATURE [Sketcher::SketchObject] Sketch021  label="S_Workbench_AngleBrace_Holes"
  FullyConstrained = true
  MapMode = 5
  Placement = pos=(0,0,0) rot=(0.57735,0.57735,0.57735;2.0944rad)
  Support = -> [YZ_Plane024]
  expr: Constraints[2] = <<S_Workbench_Master>>.Constraints.TableDepth - 2.5 in
  expr: Constraints[7] = 28 in - 1.25 in
  sketch-geometry (3):
    g0: Circle CenterX=-698.5 CenterY=-19.05 CenterZ=0 NormalX=0 NormalY=0 NormalZ=1 AngleXU=0 Radius=3.175
    g1: Circle CenterX=-50.8 CenterY=-628.65 CenterZ=0 NormalX=0 NormalY=0 NormalZ=1 AngleXU=0 Radius=3.175
    g2: Circle CenterX=-50.8 CenterY=-679.45 CenterZ=0 NormalX=0 NormalY=0 NormalZ=1 AngleXU=0 Radius=3.175
  constraints (9):
    c: Diameter(g0) = 6.35
    c: DistanceY(g0,g-1) = 19.05
    c: DistanceX(g0,g-1) = 698.5
    c: Equal(g2,g1)
    c: Equal(g1,g0)
    c: Vertical(g1,g2)
    c: DistanceY(g2,g1) = 50.8
    c: DistanceY(g2,g-1) = 679.45
    c: DistanceX(g1,g-1) = 50.8
FEATURE [PartDesign::Pocket] Pocket006  label="POCKET_Workbench_AngleBrace_Holes"
  BaseFeature = -> Pad012
  Direction = (-1,2e-16,-3e-16)
  Length = 76.2
  Length2 = 5
  Placement = pos=(0,0,0) rot=(1,1,1;2.0944rad)
  Profile = -> Sketch021
  ReferenceAxis = -> Sketch021 [N_Axis]
  Reversed = true
  Type = 0
FEATURE [PartDesign::Body] Body011  label="B_Workbench_AngleBrace"
  Group = -> [Sketch016,Pad012,Sketch021,Pocket006]
  Origin = -> Origin024
  Tip = -> Pocket006
COMPONENT P11 — recipe-attached ("P_Workbench_FrontLeg_Template", modeled in this document).
Construction recipe (the document's own serialized feature program — sketch geometry with constraints, then the solid features built on it; lengths are millimeters unless a unit is written):

FEATURE [Sketcher::SketchObject] Sketch022  label="S_Workbench_FrontLeg_Template_Holes"
  FullyConstrained = true
  MapMode = 5
  Support = -> [XY_Plane026]
  expr: Constraints[10] = <<S_Workbench_Master>>.Constraints.TwobyfourHeight
  expr: Constraints[9] = 1 mm
  sketch-geometry (4):
    g0: Circle CenterX=6.35 CenterY=63.5 CenterZ=0 NormalX=0 NormalY=0 NormalZ=1 AngleXU=0 Radius=0.5
    g1: Circle CenterX=6.35 CenterY=25.4 CenterZ=0 NormalX=0 NormalY=0 NormalZ=1 AngleXU=0 Radius=0.5
    g2: Circle CenterX=6.35 CenterY=152.4 CenterZ=0 NormalX=0 NormalY=0 NormalZ=1 AngleXU=0 Radius=0.5
    g3: Circle CenterX=6.35 CenterY=114.3 CenterZ=0 NormalX=0 NormalY=0 NormalZ=1 AngleXU=0 Radius=0.5
  constraints (12):
    c: Equal(g0,g1)
    c: Equal(g1,g2)
    c: Equal(g2,g3)
    c: Vertical(g0,g1)
    c: Vertical(g1,g2)
    c: Vertical(g2,g3)
    c: DistanceX(g-1,g3) = 6.35
    c: DistanceY(g3,g2) = 38.1
    c: DistanceY(g1,g0) = 38.1
    c: Diameter(g2) = 1
    c: DistanceY(g0,g2) = 88.9
    c: DistanceY(g-1,g1) = 25.4
FEATURE [Sketcher::SketchObject] Sketch023  label="S_Workbench_FrontLeg_Template_Body"
  FullyConstrained = true
  MapMode = 5
  Support = -> [XY_Plane026]
  expr: Constraints[8] = <<S_Workbench_Master>>.Constraints.TwobyfourHeight / 2
  sketch-geometry (4):
    g0: LineSegment StartX=0 StartY=177.8 StartZ=0 EndX=44.45 EndY=177.8 EndZ=0
    g1: LineSegment StartX=44.45 StartY=177.8 StartZ=0 EndX=44.45 EndY=0 EndZ=0
    g2: LineSegment StartX=44.45 StartY=0 StartZ=0 EndX=0 EndY=0 EndZ=0
    g3: LineSegment StartX=0 StartY=0 StartZ=0 EndX=0 EndY=177.8 EndZ=0
  constraints (11):
    c: Coincident(g0,g1)
    c: Coincident(g1,g2)
    c: Coincident(g2,g3)
    c: Coincident(g3,g0)
    c: Horizontal(g0)
    c: Horizontal(g2)
    c: Vertical(g1)
    c: Vertical(g3)
    c: DistanceX(g2,g2) = 44.45
    c: DistanceY(g1,g1) = 177.8
    c: Coincident(g2,g-1)
FEATURE [PartDesign::Pad] Pad013  label="PAD_Workbench_FrontLeg_Template_Body"
  Direction = (0,0,1)
  Length = 2
  Length2 = 10
  Profile = -> Sketch023
  ReferenceAxis = -> Sketch023 [N_Axis]
  Type = 0
  expr: Length = 2 mm
FEATURE [Sketcher::SketchObject] Sketch024  label="S_Workbench_FrontLeg_Template_Alignment"
  FullyConstrained = true
  MapMode = 5
  Support = -> [XY_Plane026]
  expr: Constraints[15] = <<S_Workbench_Master>>.Constraints.TwobyfourHeight / 2
  expr: Constraints[16] = <<S_Workbench_Master>>.Constraints.TwobyfourHeight / 2
  sketch-geometry (6):
    g0: LineSegment StartX=0 StartY=177.8 StartZ=0 EndX=0 EndY=184.15 EndZ=0
    g1: LineSegment StartX=0 StartY=184.15 StartZ=0 EndX=50.8 EndY=184.15 EndZ=0
    g2: LineSegment StartX=50.8 StartY=184.15 StartZ=0 EndX=50.8 EndY=0 EndZ=0
    g3: LineSegment StartX=50.8 StartY=0 StartZ=0 EndX=44.45 EndY=0 EndZ=0
    g4: LineSegment StartX=44.45 StartY=0 StartZ=0 EndX=44.45 EndY=177.8 EndZ=0
    g5: LineSegment StartX=0 StartY=177.8 StartZ=0 EndX=44.45 EndY=177.8 EndZ=0
  constraints (18):
    c: Coincident(g0,g1)
    c: Horizontal(g1)
    c: Vertical(g0)
    c: Coincident(g2,g3)
    c: Coincident(g3,g4)
    c: Vertical(g2)
    c: Vertical(g4)
    c: DistanceX(g3,g3) = 6.35
    c: Coincident(g5,g0)
    c: Coincident(g5,g4)
    c: Horizontal(g5)
    c: Coincident(g1,g2)
    c: DistanceY(g4,g4) = 177.8
    c: Horizontal(g3)
    c: Horizontal(g3,g-1)
    c: DistanceX(g-1,g3) = 44.45
    c: DistanceX(g5,g5) = 44.45
    c: Equal(g0,g3)
FEATURE [PartDesign::Pad] Pad014  label="PAD_Workbench_FrontLeg_Template_Alignment"
  BaseFeature = -> Pad013
  Direction = (0,0,1)
  Length = 8
  Length2 = 10
  Profile = -> Sketch024
  ReferenceAxis = -> Sketch024 [N_Axis]
  Type = 0
  expr: Length = 8 mm
FEATURE [PartDesign::Pocket] Pocket007  label="POCKET_Workbench_FrontLeg_Template_Holes"
  BaseFeature = -> Pad014
  Direction = (0,0,-1)
  Length = 12.7
  Length2 = 5
  Profile = -> Sketch022
  ReferenceAxis = -> Sketch022 [N_Axis]
  Reversed = true
  Type = 0
FEATURE [Part::Part2DObjectPython] ShapeString005  label="TEXT_Workbench_FrontLeg_Template_Label0"  # Draft 2D object (typed FeaturePython)
  FontFile = <userpath>/3dPrinting/workshop/OpenSans-Bold.ttf
  MakeFace = true
  Placement = pos=(40.0304,140.106,-0.254) rot=(0,1,0;3.14159rad)
  Size = 10.0076
  String = Front
  Tracking = 0
FEATURE [PartDesign::Pocket] Pocket016  label="POCKET_Workbench_FrontLeg_Template_Label0"
  BaseFeature = -> Pocket007
  Direction = (-2.98023e-07,-3.95e-14,1)
  Length = 1
  Length2 = 5
  Profile = -> ShapeString005
  ReferenceAxis = -> ShapeString005 [N_Axis]
  Type = 0
  expr: Length = 1 mm
FEATURE [Part::Part2DObjectPython] ShapeString006  label="TEXT_Workbench_FrontLeg_Template_Label1"  # Draft 2D object (typed FeaturePython)
  FontFile = <userpath>/3dPrinting/workshop/OpenSans-Bold.ttf
  MakeFace = true
  Placement = pos=(39.6494,124.206,0) rot=(0,1,0;3.14159rad)
  Size = 10.0076
  String = Leg
  Tracking = 0
FEATURE [PartDesign::Pocket] Pocket017  label="POCKET_Workbench_FrontLeg_Template_Label1"
  BaseFeature = -> Pocket016
  Direction = (0,0,1)
  Length = 1
  Length2 = 5
  Profile = -> ShapeString006
  ReferenceAxis = -> ShapeString006 [N_Axis]
  Type = 0
  expr: Length = 1 mm
FEATURE [PartDesign::Body] Body012  label="B_Workbench_FrontLeg_Template"
  Group = -> [Sketch022,Sketch023,Pad013,Sketch024,Pad014,Pocket007,ShapeString005,Pocket016,ShapeString006,Pocket017]
  Origin = -> Origin026
  Tip = -> Pocket017
COMPONENT P12 — recipe-attached ("P_Workbench_SideBrace_Template_Left", modeled in this document).
Construction recipe (the document's own serialized feature program — sketch geometry with constraints, then the solid features built on it; lengths are millimeters unless a unit is written):

FEATURE [Sketcher::SketchObject] Sketch025  label="S_Workbench_SideBrace_Template_Left_Base"
  FullyConstrained = true
  MapMode = 5
  Support = -> [XY_Plane028]
  expr: Constraints[10] = <<S_Workbench_Master>>.Constraints.TwobyfourHeight
  sketch-geometry (4):
    g0: LineSegment StartX=0 StartY=0 StartZ=0 EndX=-63.5 EndY=0 EndZ=0
    g1: LineSegment StartX=-63.5 StartY=0 StartZ=0 EndX=-63.5 EndY=88.9 EndZ=0
    g2: LineSegment StartX=-63.5 StartY=88.9 StartZ=0 EndX=0 EndY=88.9 EndZ=0
    g3: LineSegment StartX=0 StartY=88.9 StartZ=0 EndX=0 EndY=0 EndZ=0
  constraints (11):
    c: Coincident(g0,g1)
    c: Coincident(g1,g2)
    c: Coincident(g2,g3)
    c: Coincident(g3,g0)
    c: Horizontal(g0)
    c: Horizontal(g2)
    c: Vertical(g1)
    c: Vertical(g3)
    c: Coincident(g0,g-1)
    c: DistanceX(g2,g2) = 63.5
    c: DistanceY(g3,g3) = 88.9
FEATURE [PartDesign::Pad] Pad015  label="PAD_Workbench_SideBrace_Template_Base_Left"
  Direction = (0,0,1)
  Length = 2
  Length2 = 10
  Profile = -> Sketch025
  ReferenceAxis = -> Sketch025 [N_Axis]
  Type = 0
  expr: Length = 2 mm
FEATURE [Sketcher::SketchObject] Sketch026  label="S_Workbench_SideBrace_Template_Left_Holes"
  FullyConstrained = true
  MapMode = 5
  Support = -> [XY_Plane028]
  expr: Constraints[0] = Sketch009.Constraints.TwobyfourHeight - 2 in
  expr: Constraints[4] = 1 mm
  sketch-geometry (2):
    g0: Circle CenterX=-50.8 CenterY=63.5 CenterZ=0 NormalX=0 NormalY=0 NormalZ=1 AngleXU=0 Radius=0.5
    g1: Circle CenterX=-50.8 CenterY=25.4 CenterZ=0 NormalX=0 NormalY=0 NormalZ=1 AngleXU=0 Radius=0.5
  constraints (6):
    c: DistanceY(g1,g0) = 38.1
    c: Vertical(g0,g1)
    c: DistanceX(g1,g-1) = 50.8
    c: Equal(g0,g1)
    c: Diameter(g0) = 1
    c: DistanceY(g-1,g1) = 25.4
FEATURE [PartDesign::Pocket] Pocket008  label="POCKET_Workbench_SideBrace_Template_Left_Holes"
  BaseFeature = -> Pad015
  Direction = (0,0,-1)
  Length = 5
  Length2 = 5
  Profile = -> Sketch026
  ReferenceAxis = -> Sketch026 [N_Axis]
  Reversed = true
  Type = 1
FEATURE [Sketcher::SketchObject] Sketch027  label="S_Workbench_SideBrace_Template_Left_Alignment"
  FullyConstrained = true
  MapMode = 5
  Support = -> [XY_Plane028]
  sketch-geometry (6):
    g0: LineSegment StartX=6.35 StartY=0 StartZ=0 EndX=6.35 EndY=95.25 EndZ=0
    g1: LineSegment StartX=0 StartY=88.9 StartZ=0 EndX=0 EndY=0 EndZ=0
    g2: LineSegment StartX=0 StartY=0 StartZ=0 EndX=6.35 EndY=0 EndZ=0
    g3: LineSegment StartX=-63.5 StartY=88.9 StartZ=0 EndX=0 EndY=88.9 EndZ=0
    g4: LineSegment StartX=-63.5 StartY=88.9 StartZ=0 EndX=-63.5 EndY=95.25 EndZ=0
    g5: LineSegment StartX=-63.5 StartY=95.25 StartZ=0 EndX=6.35 EndY=95.25 EndZ=0
  constraints (17):
    c: PointOnObject(g1,g-2)
    c: Vertical(g0)
    c: DistanceX(g-1,g0) = 6.35
    c: Horizontal(g0,g1)
    c: Coincident(g2,g1)
    c: Coincident(g2,g0)
    c: Coincident(g1,g-1)
    c: Coincident(g3,g1)
    c: Horizontal(g3)
    c: DistanceY(g1,g1) = 88.9
    c: Coincident(g4,g3)
    c: Coincident(g5,g0)
    c: Horizontal(g5)
    c: Vertical(g4)
    c: Equal(g4,g2)
    c: Coincident(g4,g5)
    c: DistanceX(g3,g3) = 63.5
FEATURE [PartDesign::Pad] Pad016  label="PAD_Workbench_SideBrace_Template_Left_Alignment"
  BaseFeature = -> Pocket008
  Direction = (0,0,1)
  Length = 8
  Length2 = 10
  Profile = -> Sketch027
  ReferenceAxis = -> Sketch027 [N_Axis]
  Type = 0
  expr: Length = 8 mm
FEATURE [Part::Part2DObjectPython] ShapeString007  label="TEXT_Workbench_SideBrace_Template_Left_SideBrace"  # Draft 2D object (typed FeaturePython)
  FontFile = <userpath>/3dPrinting/workshop/OpenSans-Bold.ttf
  MakeFace = true
  Placement = pos=(-3.72384e-06,42.5958,0) rot=(0,1,0;3.14159rad)
  Size = 10.0076
  String = Side Brace
  Tracking = 0
FEATURE [PartDesign::Pocket] Pocket018  label="POCKET_Workbench_SideBrace_Template_Left_SideBrace"
  BaseFeature = -> Pad016
  Direction = (0,0,1)
  Length = 1
  Length2 = 5
  Profile = -> ShapeString007
  ReferenceAxis = -> ShapeString007 [N_Axis]
  Type = 0
  expr: Length = 1 mm
FEATURE [Part::Part2DObjectPython] ShapeString008  label="TEXT_Workbench_SideBrace_Template_Left_Left"  # Draft 2D object (typed FeaturePython)
  FontFile = <userpath>/3dPrinting/workshop/OpenSans-Bold.ttf
  MakeFace = true
  Placement = pos=(-2.68463e-06,30.7086,0) rot=(0,1,0;3.14159rad)
  Size = 10.0076
  String = Left
  Tracking = 0
FEATURE [PartDesign::Pocket] Pocket019  label="POCKET_Workbench_SideBrace_Template_Left_Left"
  BaseFeature = -> Pocket018
  Direction = (0,0,1)
  Length = 1
  Length2 = 5
  Profile = -> ShapeString008
  ReferenceAxis = -> ShapeString008 [N_Axis]
  Type = 0
  expr: Length = 1 mm
FEATURE [PartDesign::Body] Body013  label="B_Workbench_SideBrace_Template_Left"
  Group = -> [Sketch025,Pad015,Sketch026,Pocket008,Sketch027,Pad016,ShapeString007,Pocket018,ShapeString008,Pocket019]
  Origin = -> Origin028
  Tip = -> Pocket019
COMPONENT P13 — recipe-attached ("P_Workbench_BackShelf_Template", modeled in this document).
Construction recipe (the document's own serialized feature program — sketch geometry with constraints, then the solid features built on it; lengths are millimeters unless a unit is written):

FEATURE [Sketcher::SketchObject] Sketch028  label="S_Workbench_BackShelf_Template_Base"
  FullyConstrained = true
  MapMode = 5
  Support = -> [XY_Plane030]
  sketch-geometry (4):
    g0: LineSegment StartX=0 StartY=127 StartZ=0 EndX=101.6 EndY=127 EndZ=0
    g1: LineSegment StartX=101.6 StartY=127 StartZ=0 EndX=101.6 EndY=0 EndZ=0
    g2: LineSegment StartX=101.6 StartY=0 StartZ=0 EndX=0 EndY=0 EndZ=0
    g3: LineSegment StartX=0 StartY=0 StartZ=0 EndX=0 EndY=127 EndZ=0
  constraints (12):
    c: Coincident(g0,g1)
    c: Coincident(g1,g2)
    c: Coincident(g2,g3)
    c: Coincident(g3,g0)
    c: Horizontal(g0)
    c: Horizontal(g2)
    c: Vertical(g1)
    c: Vertical(g3)
    c: PointOnObject(g0,g-2)
    c: PointOnObject(g1,g-1)
    c: DistanceY(g1,g1) = 127
    c: DistanceX(g0,g0) = 101.6
FEATURE [PartDesign::Pad] Pad017  label="PAD_Workbench_BackShelf_Template_Base"
  Direction = (0,0,1)
  Length = 2
  Length2 = 10
  Profile = -> Sketch028
  ReferenceAxis = -> Sketch028 [N_Axis]
  Type = 0
  expr: Length = 2 mm
FEATURE [Sketcher::SketchObject] Sketch029  label="S_Workbench_BackShelf_Template_Holes"
  FullyConstrained = true
  MapMode = 5
  Support = -> [XY_Plane030]
  expr: Constraints[2] = 1 mm
  sketch-geometry (3):
    g0: Circle CenterX=50.8 CenterY=114.3 CenterZ=0 NormalX=0 NormalY=0 NormalZ=1 AngleXU=0 Radius=0.5
    g1: Circle CenterX=50.8 CenterY=38.1 CenterZ=0 NormalX=0 NormalY=0 NormalZ=1 AngleXU=0 Radius=0.5
    g2: GeomPoint X=50.8 Y=127 Z=0
  constraints (8):
    c: Vertical(g0,g1)
    c: Equal(g0,g1)
    c: Diameter(g0) = 1
    c: DistanceY(g1,g0) = 76.2
    c: DistanceX(g-1,g1) = 50.8
    c: Vertical(g2,g0)
    c: DistanceY(g-1,g2) = 127
    c: DistanceY(g0,g2) = 12.7
FEATURE [PartDesign::Pocket] Pocket009  label="POCKET_Workbench_BackShelf_Template_Holes"
  BaseFeature = -> Pad017
  Direction = (0,0,-1)
  Length = 5.0038
  Length2 = 5
  Profile = -> Sketch029
  ReferenceAxis = -> Sketch029 [N_Axis]
  Reversed = true
  Type = 0
FEATURE [Sketcher::SketchObject] Sketch030  label="S_Workbench_BackShelf_Template_Alignment"
  FullyConstrained = true
  MapMode = 5
  Support = -> [XY_Plane030]
  sketch-geometry (4):
    g0: LineSegment StartX=107.95 StartY=127 StartZ=0 EndX=101.6 EndY=127 EndZ=0
    g1: LineSegment StartX=101.6 StartY=127 StartZ=0 EndX=101.6 EndY=0 EndZ=0
    g2: LineSegment StartX=101.6 StartY=0 StartZ=0 EndX=107.95 EndY=0 EndZ=0
    g3: LineSegment StartX=107.95 StartY=0 StartZ=0 EndX=107.95 EndY=127 EndZ=0
  constraints (12):
    c: Coincident(g0,g1)
    c: Coincident(g1,g2)
    c: Coincident(g2,g3)
    c: Coincident(g3,g0)
    c: Horizontal(g0)
    c: Horizontal(g2)
    c: Vertical(g1)
    c: Vertical(g3)
    c: PointOnObject(g1,g-1)
    c: DistanceX(g2,g2) = 6.35
    c: DistanceY(g3,g3) = 127
    c: DistanceX(g-1,g1) = 101.6
FEATURE [PartDesign::Pad] Pad018  label="PAD_Workbench_BackShelf_Template_Alignment"
  BaseFeature = -> Pocket009
  Direction = (0,0,1)
  Length = 8
  Length2 = 10
  Profile = -> Sketch030
  ReferenceAxis = -> Sketch030 [N_Axis]
  Type = 0
  expr: Length = 8 mm
FEATURE [Part::Part2DObjectPython] ShapeString001  label="TEXT_Workbench_BackShelf_Template_Label0"  # Draft 2D object (typed FeaturePython)
  FontFile = <path>
  MakeFace = true
  Placement = pos=(84.201,86.1822,1e-14) rot=(0,1,0;3.14159rad)
  Size = 10.0076
  String = Back Leg
  Tracking = 0
FEATURE [PartDesign::Pocket] Pocket012  label="POCKET_Workbench_BackShelf_Template_Label0"
  BaseFeature = -> Pad018
  Direction = (0,0,1)
  Length = 1
  Length2 = 5
  Profile = -> ShapeString001
  ReferenceAxis = -> ShapeString001 [N_Axis]
  Type = 0
  expr: Length = 1 mm
FEATURE [Part::Part2DObjectPython] ShapeString002  label="TEXT_Workbench_BackShelf_Template_Label1"  # Draft 2D object (typed FeaturePython)
  FontFile = <path>
  MakeFace = true
  Placement = pos=(84.201,75.2856,1e-14) rot=(0,1,0;3.14159rad)
  Size = 10.0076
  String = Shelf Holes
  Tracking = 0
FEATURE [PartDesign::Pocket] Pocket013  label="POCKET_Workbench_BackShelf_Template_Label1"
  BaseFeature = -> Pocket012
  Direction = (0,0,1)
  Length = 1
  Length2 = 5
  Profile = -> ShapeString002
  ReferenceAxis = -> ShapeString002 [N_Axis]
  Type = 0
  expr: Length = 1 mm
FEATURE [PartDesign::Body] Body014  label="B_Workbench_BackShelf_Template"
  Group = -> [Sketch028,Pad017,Sketch029,Pocket009,Sketch030,Pad018,ShapeString001,Pocket012,ShapeString002,Pocket013]
  Origin = -> Origin030
  Tip = -> Pocket013
COMPONENT P14 — recipe-attached ("P_Workbench_ShelfBrace_Template", modeled in this document).
Construction recipe (the document's own serialized feature program — sketch geometry with constraints, then the solid features built on it; lengths are millimeters unless a unit is written):

FEATURE [Sketcher::SketchObject] Sketch031  label="S_Workbench_ShelfBrace_Template_Base"
  FullyConstrained = true
  MapMode = 5
  Support = -> [XY_Plane032]
  expr: Constraints[10] = <<S_Workbench_Master>>.Constraints.ShelfDepth
  expr: Constraints[1] = <<S_Workbench_Master>>.Constraints.ShelfDepth / 2
  sketch-geometry (7):
    g0: LineSegment StartX=0 StartY=-190.5 StartZ=0 EndX=0 EndY=0 EndZ=0
    g1: LineSegment StartX=0 StartY=0 StartZ=0 EndX=-76.2 EndY=0 EndZ=0
    g2: GeomPoint X=-381 Y=0 Z=0
    g3: LineSegment StartX=-381 StartY=0 StartZ=0 EndX=-76.2 EndY=0 EndZ=0
    g4: LineSegment StartX=-381 StartY=0 StartZ=0 EndX=-76.2 EndY=-152.4 EndZ=0
    g5: LineSegment StartX=-76.2 StartY=-152.4 StartZ=0 EndX=0 EndY=-190.5 EndZ=0
    g6: LineSegment StartX=-76.2 StartY=0 StartZ=0 EndX=-76.2 EndY=-152.4 EndZ=0
  constraints (16):
    c: PointOnObject(g0,g-2)
    c: DistanceY(g0,g0) = 190.5
    c: Coincident(g1,g0)
    c: PointOnObject(g1,g-1)
    c: PointOnObject(g2,g-1)
    c: Coincident(g3,g2)
    c: Coincident(g3,g1)
    c: Coincident(g4,g3)
    c: Coincident(g5,g0)
    c: Tangent(g5,g4) = -1.5708
    c: DistanceX(g3,g0) = 381
    c: Coincident(g0,g-1)
    c: Coincident(g6,g1)
    c: Coincident(g6,g4)
    c: Vertical(g6)
    c: DistanceX(g1,g0) = 76.2
FEATURE [PartDesign::Pad] Pad019  label="PAD_Workbench_ShelfBrace_Template_Base"
  Direction = (0,0,1)
  Length = 2
  Length2 = 10
  Profile = -> Sketch031
  ReferenceAxis = -> Sketch031 [N_Axis]
  Type = 0
FEATURE [Sketcher::SketchObject] Sketch032  label="S_Workbench_ShelfBrace_Template_Holes"
  FullyConstrained = true
  MapMode = 5
  Support = -> [XY_Plane032]
  expr: Constraints[1] = 1 mm
  sketch-geometry (2):
    g0: Circle CenterX=-50.8 CenterY=-25.4 CenterZ=0 NormalX=0 NormalY=0 NormalZ=1 AngleXU=0 Radius=0.5
    g1: Circle CenterX=-50.8 CenterY=-101.6 CenterZ=0 NormalX=0 NormalY=0 NormalZ=1 AngleXU=0 Radius=0.5
  constraints (6):
    c: Equal(g1,g0)
    c: Diameter(g0) = 1
    c: Vertical(g0,g1)
    c: DistanceY(g1,g0) = 76.2
    c: DistanceX(g0,g-1) = 50.8
    c: DistanceY(g0,g-1) = 25.4
FEATURE [PartDesign::Pocket] Pocket010  label="POCKET_Workbench_ShelfBrace_Template_Holes"
  BaseFeature = -> Pad019
  Direction = (0,0,-1)
  Length = 5
  Length2 = 5
  Profile = -> Sketch032
  ReferenceAxis = -> Sketch032 [N_Axis]
  Reversed = true
  Type = 1
FEATURE [Sketcher::SketchObject] Sketch033  label="S_Workbench_ShelfBrace_Template_Alignment"
  FullyConstrained = true
  MapMode = 5
  Support = -> [XY_Plane032]
  expr: Constraints[13] = <<S_Workbench_Master>>.Constraints.ShelfDepth / 2
  sketch-geometry (6):
    g0: LineSegment StartX=-76.2 StartY=0 StartZ=0 EndX=-76.2 EndY=6.35 EndZ=0
    g1: LineSegment StartX=-76.2 StartY=6.35 StartZ=0 EndX=6.35 EndY=6.35 EndZ=0
    g2: LineSegment StartX=6.35 StartY=6.35 StartZ=0 EndX=6.35 EndY=-190.5 EndZ=0
    g3: LineSegment StartX=6.35 StartY=-190.5 StartZ=0 EndX=0 EndY=-190.5 EndZ=0
    g4: LineSegment StartX=0 StartY=-190.5 StartZ=0 EndX=0 EndY=0 EndZ=0
    g5: LineSegment StartX=0 StartY=0 StartZ=0 EndX=-76.2 EndY=0 EndZ=0
  constraints (17):
    c: PointOnObject(g0,g-1)
    c: Vertical(g0)
    c: Coincident(g0,g1)
    c: Horizontal(g1)
    c: Coincident(g2,g1)
    c: Vertical(g2)
    c: PointOnObject(g3,g-2)
    c: Coincident(g4,g3)
    c: Coincident(g4,g-1)
    c: Coincident(g5,g4)
    c: Coincident(g5,g0)
    c: Coincident(g3,g2)
    c: Horizontal(g3)
    c: DistanceY(g4,g4) = 190.5
    c: DistanceX(g5,g5) = 76.2
    c: Equal(g3,g0)
    c: DistanceY(g0,g0) = 6.35
FEATURE [PartDesign::Pad] Pad020  label="PAD_Workbench_ShelfBrace_Template_Alignment"
  BaseFeature = -> Pocket010
  Direction = (0,0,1)
  Length = 8
  Length2 = 10
  Profile = -> Sketch033
  ReferenceAxis = -> Sketch033 [N_Axis]
  Type = 0
  expr: Length = 8 mm
FEATURE [Part::Part2DObjectPython] ShapeString  label="TEXT_Workbench_ShelfBrace_Template_Label"  # Draft 2D object (typed FeaturePython)
  FontFile = <path>
  MakeFace = true
  Placement = pos=(-1.9812,-57.7088,-1e-15) rot=(0,1,0;3.14159rad)
  Size = 10.0076
  String = Shelf Brace
  Tracking = 0
FEATURE [PartDesign::Pocket] Pocket011  label="POCKET_Workbench_ShelfBrace_Template_Label"
  BaseFeature = -> Pad020
  Direction = (0,0,1)
  Length = 1
  Length2 = 5
  Profile = -> ShapeString
  ReferenceAxis = -> ShapeString [N_Axis]
  Type = 0
  expr: Length = 1 mm
FEATURE [PartDesign::Body] Body015  label="B_Workbench_ShelfBrace_Template"
  Group = -> [Sketch031,Pad019,Sketch032,Pocket010,Sketch033,Pad020,ShapeString,Pocket011]
  Origin = -> Origin032
  Tip = -> Pocket011
COMPONENT P15 — recipe-attached ("P_Workbench_SideBrace_Template_Right", modeled in this document).
Construction recipe (the document's own serialized feature program — sketch geometry with constraints, then the solid features built on it; lengths are millimeters unless a unit is written):

FEATURE [Sketcher::SketchObject] Sketch034  label="S_Workbench_SideBrace_Template_Right_Base"
  FullyConstrained = true
  MapMode = 5
  Support = -> [XY_Plane034]
  sketch-geometry (4):
    g0: LineSegment StartX=0 StartY=0 StartZ=0 EndX=-63.5 EndY=0 EndZ=0
    g1: LineSegment StartX=-63.5 StartY=0 StartZ=0 EndX=-63.5 EndY=88.9 EndZ=0
    g2: LineSegment StartX=-63.5 StartY=88.9 StartZ=0 EndX=0 EndY=88.9 EndZ=0
    g3: LineSegment StartX=0 StartY=88.9 StartZ=0 EndX=0 EndY=0 EndZ=0
  constraints (11):
    c: Coincident(g0,g1)
    c: Coincident(g1,g2)
    c: Coincident(g2,g3)
    c: Coincident(g3,g0)
    c: Horizontal(g0)
    c: Horizontal(g2)
    c: Vertical(g1)
    c: Vertical(g3)
    c: Coincident(g0,g-1)
    c: DistanceX(g2,g2) = 63.5
    c: DistanceY(g1,g1) = 88.9
FEATURE [PartDesign::Pad] Pad021  label="PAD_Workbench_SideBrace_Template_Right_Base"
  Direction = (0,0,1)
  Length = 2
  Length2 = 10
  Profile = -> Sketch034
  ReferenceAxis = -> Sketch034 [N_Axis]
  Type = 0
  expr: Length = 2 mm
FEATURE [Sketcher::SketchObject] Sketch035  label="S_Workbench_SideBrace_Template_Right_Alignment"
  FullyConstrained = true
  MapMode = 5
  Support = -> [XY_Plane034]
  sketch-geometry (6):
    g0: LineSegment StartX=-63.5 StartY=0 StartZ=0 EndX=-63.5 EndY=88.9 EndZ=0
    g1: LineSegment StartX=0 StartY=88.9 StartZ=0 EndX=0 EndY=95.25 EndZ=0
    g2: LineSegment StartX=0 StartY=95.25 StartZ=0 EndX=-69.85 EndY=95.25 EndZ=0
    g3: LineSegment StartX=-63.5 StartY=88.9 StartZ=0 EndX=0 EndY=88.9 EndZ=0
    g4: LineSegment StartX=-69.85 StartY=95.25 StartZ=0 EndX=-69.85 EndY=0 EndZ=0
    g5: LineSegment StartX=-69.85 StartY=0 StartZ=0 EndX=-63.5 EndY=0 EndZ=0
  constraints (18):
    c: PointOnObject(g0,g-1)
    c: Vertical(g0)
    c: PointOnObject(g1,g-2)
    c: PointOnObject(g1,g-2)
    c: Coincident(g2,g1)
    c: Horizontal(g2)
    c: Coincident(g3,g0)
    c: Coincident(g3,g1)
    c: Horizontal(g3)
    c: Coincident(g4,g2)
    c: PointOnObject(g4,g-1)
    c: Coincident(g5,g4)
    c: Coincident(g5,g0)
    c: Vertical(g4)
    c: DistanceY(g0,g0) = 88.9
    c: DistanceX(g3,g3) = 63.5
    c: Equal(g1,g5)
    c: DistanceX(g5,g5) = 6.35
FEATURE [PartDesign::Pad] Pad022  label="PAD_Workbench_SideBrace_Template_Right_Alignment"
  BaseFeature = -> Pad021
  Direction = (0,0,1)
  Length = 8
  Length2 = 10
  Profile = -> Sketch035
  ReferenceAxis = -> Sketch035 [N_Axis]
  Type = 0
  expr: Length = 8 mm
FEATURE [Sketcher::SketchObject] Sketch036  label="S_Workbench_SideBrace_Template_Right_Holes"
  FullyConstrained = true
  MapMode = 5
  Support = -> [XY_Plane034]
  expr: Constraints[2] = 3.5 in - 1 in
  expr: Constraints[5] = 1 mm
  sketch-geometry (2):
    g0: Circle CenterX=-12.7 CenterY=63.5 CenterZ=0 NormalX=0 NormalY=0 NormalZ=1 AngleXU=0 Radius=0.5
    g1: Circle CenterX=-12.7 CenterY=25.4 CenterZ=0 NormalX=0 NormalY=0 NormalZ=1 AngleXU=0 Radius=0.5
  constraints (6):
    c: Equal(g0,g1)
    c: DistanceY(g1,g0) = 38.1
    c: DistanceY(g-1,g0) = 63.5
    c: Vertical(g0,g1)
    c: DistanceX(g1,g-1) = 12.7
    c: Diameter(g1) = 1
FEATURE [PartDesign::Pocket] Pocket020  label="POCKET_Workbench_SideBrace_Template_Right_Holes"
  BaseFeature = -> Pad022
  Direction = (0,0,-1)
  Length = 5.0038
  Length2 = 5
  Profile = -> Sketch036
  ReferenceAxis = -> Sketch036 [N_Axis]
  Reversed = true
  Type = 0
FEATURE [Part::Part2DObjectPython] ShapeString009  label="TEXT_Workbench_SideBrace_Template_Right_Label0"  # Draft 2D object (typed FeaturePython)
  FontFile = <userpath>/3dPrinting/workshop/OpenSans-Bold.ttf
  MakeFace = true
  Placement = pos=(-4.953,48.5394,-0.0254) rot=(0,1,0;3.14159rad)
  Size = 10.0076
  String = Side Brace
  Tracking = 0
FEATURE [Part::Part2DObjectPython] ShapeString010  label="_Workbench_SideBrace_Template_Right_Label1"  # Draft 2D object (typed FeaturePython)
  FontFile = <userpath>/3dPrinting/workshop/OpenSans-Bold.ttf
  MakeFace = true
  Placement = pos=(-4.953,36.6522,-0.254) rot=(0,1,0;3.14159rad)
  Size = 10.0076
  String = Right
  Tracking = 0
FEATURE [PartDesign::Pocket] Pocket021  label="POCKET_Workbench_SideBrace_Template_Right_Label0"
  BaseFeature = -> Pocket020
  Direction = (-2.98023e-07,0,1)
  Length = 1
  Length2 = 5
  Profile = -> ShapeString009
  ReferenceAxis = -> ShapeString009 [N_Axis]
  Type = 0
  expr: Length = 1 mm
FEATURE [PartDesign::Pocket] Pocket022  label="POCKET_Workbench_SideBrace_Template_Right_Label1"
  BaseFeature = -> Pocket021
  Direction = (-2.98023e-07,0,1)
  Length = 1
  Length2 = 5
  Profile = -> ShapeString010
  ReferenceAxis = -> ShapeString010 [N_Axis]
  Type = 0
  expr: Length = 1 mm
FEATURE [PartDesign::Body] Body016  label="B_Workbench_SideBrace_Template_Right"
  Group = -> [Sketch034,Pad021,Sketch035,Pad022,Sketch036,Pocket020,ShapeString009,ShapeString010,Pocket021,Pocket022]
  Origin = -> Origin034
  Tip = -> Pocket022
COMPONENT P16 — recipe-attached ("P_Workbench_CutList_2x4_BackLeg", modeled in this document).
Construction recipe (the document's own serialized feature program — sketch geometry with constraints, then the solid features built on it; lengths are millimeters unless a unit is written):

FEATURE [Sketcher::SketchObject] Sketch037
  FullyConstrained = true
  MapMode = 5
  Support = -> [XY_Plane037]
  expr: Constraints[8] = <<S_Workbench_Master>>.Constraints.TwobyfourWidth
  expr: Constraints[9] = <<S_Workbench_Master>>.Constraints.TwobyfourHeight
  sketch-geometry (4):
    g0: LineSegment StartX=-19.05 StartY=44.45 StartZ=0 EndX=19.05 EndY=44.45 EndZ=0
    g1: LineSegment StartX=19.05 StartY=44.45 StartZ=0 EndX=19.05 EndY=-44.45 EndZ=0
    g2: LineSegment StartX=19.05 StartY=-44.45 StartZ=0 EndX=-19.05 EndY=-44.45 EndZ=0
    g3: LineSegment StartX=-19.05 StartY=-44.45 StartZ=0 EndX=-19.05 EndY=44.45 EndZ=0
  constraints (11):
    c: Coincident(g0,g1)
    c: Coincident(g1,g2)
    c: Coincident(g2,g3)
    c: Coincident(g3,g0)
    c: Horizontal(g0)
    c: Horizontal(g2)
    c: Vertical(g1)
    c: Vertical(g3)
    c: DistanceX(g0,g0) = 38.1
    c: DistanceY(g1,g1) = 88.9
    c: Symmetric(g0,g1,g-1)
FEATURE [PartDesign::Pad] Pad023
  Direction = (0,0,1)
  Length = 457.2
  Length2 = 10
  Profile = -> Sketch037
  ReferenceAxis = -> Sketch037 [N_Axis]
  Type = 0
  expr: Length = 96 in - <<S_Workbench_Master>>.Constraints.BackLegHeight
FEATURE [PartDesign::Body] Body018  label="B_Workbench_CutList_2x4_Waste"
  Group = -> [Sketch037,Pad023]
  Origin = -> Origin037
  Placement = pos=(0,0,2006.6) rot=(0,0,1;0rad)
  Tip = -> Pad023
FEATURE [Sketcher::SketchObject] Sketch038
  FullyConstrained = true
  MapMode = 5
  Support = -> [XY_Plane036]
  expr: Constraints[10] = <<S_Workbench_Master>>.Constraints.TwobyfourHeight
  expr: Constraints[9] = <<S_Workbench_Master>>.Constraints.TwobyfourWidth
  sketch-geometry (4):
    g0: LineSegment StartX=-19.05 StartY=44.45 StartZ=0 EndX=19.05 EndY=44.45 EndZ=0
    g1: LineSegment StartX=19.05 StartY=44.45 StartZ=0 EndX=19.05 EndY=-44.45 EndZ=0
    g2: LineSegment StartX=19.05 StartY=-44.45 StartZ=0 EndX=-19.05 EndY=-44.45 EndZ=0
    g3: LineSegment StartX=-19.05 StartY=-44.45 StartZ=0 EndX=-19.05 EndY=44.45 EndZ=0
  constraints (11):
    c: Coincident(g0,g1)
    c: Coincident(g1,g2)
    c: Coincident(g2,g3)
    c: Coincident(g3,g0)
    c: Horizontal(g0)
    c: Horizontal(g2)
    c: Vertical(g1)
    c: Vertical(g3)
    c: Symmetric(g0,g1,g-1)
    c: DistanceX(g0,g0) = 38.1
    c: DistanceY(g1,g1) = 88.9
FEATURE [PartDesign::Pad] Pad024
  Direction = (0,0,1)
  Length = 1981.2
  Length2 = 10
  Profile = -> Sketch038
  ReferenceAxis = -> Sketch038 [N_Axis]
  Type = 0
  expr: Length = <<S_Workbench_Master>>.Constraints.BackLegHeight
FEATURE [PartDesign::Body] Body017  label="B_Workbench_CutList_2x4_BackLeg"
  Group = -> [Sketch038,Pad024]
  Origin = -> Origin036
  Tip = -> Pad024
FEATURE [Part::Part2DObjectPython] Clone2D  label="S_2x4_Profile (2D)"  # Draft 2D object (typed FeaturePython)
  Fuse = false
  Objects = -> [Sketch040]
  Placement = pos=(0,304.8,0) rot=(1,0,0;0rad)
  Scale = (1,1,1)
FEATURE [PartDesign::Pad] Pad025
  Direction = (0,0,1)
  Length = 2438.4
  Length2 = 10
  Placement = pos=(0,304.8,0) rot=(1,0,0;0rad)
  Profile = -> Clone2D
  ReferenceAxis = -> Clone2D [N_Axis]
  Type = 0
FEATURE [PartDesign::Body] Body022  label="B_Workbench_CutList_2x4_Whole"
  Group = -> [Clone2D,Pad025]
  Origin = -> Origin042
  Tip = -> Pad025
COMPONENT P17 — recipe-attached ("P_Workbench_CutList_2x4_FrontLeg", modeled in this document).
Construction recipe (the document's own serialized feature program — sketch geometry with constraints, then the solid features built on it; lengths are millimeters unless a unit is written):

FEATURE [Part::Part2DObjectPython] Clone2D001  label="S_2x4_Profile (2D)001"  # Draft 2D object (typed FeaturePython)
  Fuse = false
  Objects = -> [Sketch040]
  Scale = (1,1,1)
FEATURE [Part::Part2DObjectPython] Clone2D002  label="S_2x4_Profile (2D)001 (2D)"  # Draft 2D object (typed FeaturePython)
  Fuse = false
  Objects = -> [Clone2D001]
  Scale = (1,1,1)
FEATURE [Part::Part2DObjectPython] Clone2D003  label="S_2x4_Profile (2D)001 (2D) (2D)"  # Draft 2D object (typed FeaturePython)
  Fuse = false
  Objects = -> [Clone2D002]
  Scale = (1,1,1)
FEATURE [Part::Part2DObjectPython] Clone2D004  label="S_2x4_Profile (2D)001 (2D) (2D) (2D)"  # Draft 2D object (typed FeaturePython)
  Fuse = false
  Objects = -> [Clone2D003]
  Scale = (1,1,1)
FEATURE [PartDesign::Pad] Pad026
  Direction = (0,0,1)
  Length = 723.9
  Length2 = 10
  Profile = -> Clone2D001
  ReferenceAxis = -> Clone2D001 [N_Axis]
  Type = 0
  expr: Length = <<S_Workbench_Master>>.Constraints.FrontLegHeight
FEATURE [PartDesign::Body] Body019  label="P_2x4_CutList_FrontLeg_FrontLeg"
  Group = -> [Clone2D001,Pad026]
  Origin = -> Origin039
  Tip = -> Pad026
FEATURE [PartDesign::Pad] Pad027
  Direction = (0,0,1)
  Length = 1066.8
  Length2 = 10
  Profile = -> Clone2D002
  ReferenceAxis = -> Clone2D002 [N_Axis]
  Type = 0
  expr: Length = <<S_Workbench_Master>>.Constraints.TableWidth - 4 * Sketch009.Constraints.TwobyfourWidth
FEATURE [PartDesign::Body] Body020  label="P_2x4_CutList_FrontLeg_BackBrace"
  Group = -> [Clone2D002,Pad027]
  Origin = -> Origin040
  Placement = pos=(0,0,749.3) rot=(0,0,1;0rad)
  Tip = -> Pad027
  expr: .Placement.Base.z = <<S_Workbench_Master>>.Constraints.FrontLegHeight + 1 in
FEATURE [PartDesign::Pad] Pad028
  Direction = (0,0,1)
  Length = 647.7
  Length2 = 10
  Profile = -> Clone2D003
  ReferenceAxis = -> Clone2D003 [N_Axis]
  Type = 0
  expr: Length = 96 in - <<S_Workbench_Master>>.Constraints.FrontLegHeight - (<<S_Workbench_Master>>.Constraints.TableWidth - 4 * Sketch009.Constraints.TwobyfourWidth)
FEATURE [PartDesign::Body] Body021  label="P_2x4_CutList_FrontLeg_Waste"
  Group = -> [Clone2D003,Pad028]
  Origin = -> Origin041
  Placement = pos=(0,0,1841.5) rot=(0,0,1;0rad)
  Tip = -> Pad028
  expr: .Placement.Base.z = <<S_Workbench_Master>>.Constraints.FrontLegHeight + <<S_Workbench_Master>>.Constraints.TableWidth - 4 * Sketch009.Constraints.TwobyfourWidth + 2 in
FEATURE [PartDesign::Pad] Pad029
  Direction = (0,0,1)
  Length = 2438.4
  Length2 = 10
  Profile = -> Clone2D004
  ReferenceAxis = -> Clone2D004 [N_Axis]
  Type = 0
FEATURE [PartDesign::Body] Body023  label="B_2x4_CutList_FrontLeg_Whole"
  Group = -> [Clone2D004,Pad029]
  Origin = -> Origin043
  Placement = pos=(0,304.8,0) rot=(0,0,1;0rad)
  Tip = -> Pad029
COMPONENT P18 — recipe-attached ("P_Workbench_CutList_2x4_SideBrace", modeled in this document).
Construction recipe (the document's own serialized feature program — sketch geometry with constraints, then the solid features built on it; lengths are millimeters unless a unit is written):

FEATURE [Part::Part2DObjectPython] Clone2D005  label="S_2x4_Profile (2D)002"  # Draft 2D object (typed FeaturePython)
  Fuse = false
  Objects = -> [Sketch040]
  Scale = (1,1,1)
FEATURE [Part::Part2DObjectPython] Clone2D006  label="S_2x4_Profile (2D)003"  # Draft 2D object (typed FeaturePython)
  Fuse = false
  Objects = -> [Sketch040]
  Scale = (1,1,1)
FEATURE [Part::Part2DObjectPython] Clone2D007  label="S_2x4_Profile (2D)004"  # Draft 2D object (typed FeaturePython)
  Fuse = false
  Objects = -> [Sketch040]
  Scale = (1,1,1)
FEATURE [Part::Part2DObjectPython] Clone2D008  label="S_2x4_Profile (2D)005"  # Draft 2D object (typed FeaturePython)
  Fuse = false
  Objects = -> [Sketch040]
  Scale = (1,1,1)
FEATURE [PartDesign::Pad] Pad030
  Direction = (0,0,1)
  Length = 2438.4
  Length2 = 10
  Profile = -> Clone2D008
  ReferenceAxis = -> Clone2D008 [N_Axis]
  Type = 0
FEATURE [PartDesign::Body] Body027  label="B_Workbench_CutList_2x4_SideBrace_Whole"
  Group = -> [Clone2D008,Pad030]
  Origin = -> Origin048
  Placement = pos=(0,304.8,0) rot=(0,0,1;0rad)
  Tip = -> Pad030
FEATURE [PartDesign::Pad] Pad031
  Direction = (0,0,1)
  Length = 762
  Length2 = 10
  Profile = -> Clone2D005
  ReferenceAxis = -> Clone2D005 [N_Axis]
  Type = 0
  expr: Length = <<S_Workbench_Master>>.Constraints.TableDepth
FEATURE [PartDesign::Body] Body024  label="B_Workbench_CutList_2x4_SideBrace_0"
  Group = -> [Clone2D005,Pad031]
  Origin = -> Origin045
  Tip = -> Pad031
FEATURE [PartDesign::Pad] Pad032
  Direction = (0,0,1)
  Length = 762
  Length2 = 10
  Profile = -> Clone2D006
  ReferenceAxis = -> Clone2D006 [N_Axis]
  Type = 0
  expr: Length = <<S_Workbench_Master>>.Constraints.TableDepth
FEATURE [PartDesign::Body] Body025  label="B_Workbench_CutList_2x4_SideBrace_1"
  Group = -> [Clone2D006,Pad032]
  Origin = -> Origin046
  Placement = pos=(0,0,787.4) rot=(0,0,1;0rad)
  Tip = -> Pad032
  expr: .Placement.Base.z = <<S_Workbench_Master>>.Constraints.TableDepth + 1 in
FEATURE [PartDesign::Pad] Pad033
  Direction = (0,0,1)
  Length = 914.4
  Length2 = 10
  Profile = -> Clone2D007
  ReferenceAxis = -> Clone2D007 [N_Axis]
  Type = 0
  expr: Length = 96 in - <<S_Workbench_Master>>.Constraints.TableDepth * 2
FEATURE [PartDesign::Body] Body026  label="B_Workbench_CutList_2x4_SideBrace_Waste"
  Group = -> [Clone2D007,Pad033]
  Origin = -> Origin047
  Placement = pos=(0,0,1574.8) rot=(0,0,1;0rad)
  Tip = -> Pad033
  expr: .Placement.Base.z = <<S_Workbench_Master>>.Constraints.TableDepth * 2 + 2 in
COMPONENT P19 — recipe-attached ("P_Workbench_CutList_Plywood", modeled in this document).
Construction recipe (the document's own serialized feature program — sketch geometry with constraints, then the solid features built on it; lengths are millimeters unless a unit is written):

FEATURE [Sketcher::SketchObject] Sketch042
  FullyConstrained = true
  MapMode = 5
  Support = -> [XY_Plane055]
  sketch-geometry (5):
    g0: LineSegment StartX=-1219.2 StartY=-609.6 StartZ=0 EndX=-1219.2 EndY=609.6 EndZ=0
    g1: LineSegment StartX=-1219.2 StartY=609.6 StartZ=0 EndX=1219.2 EndY=609.6 EndZ=0
    g2: LineSegment StartX=1219.2 StartY=609.6 StartZ=0 EndX=1219.2 EndY=-609.6 EndZ=0
    g3: LineSegment StartX=1219.2 StartY=-609.6 StartZ=0 EndX=-1219.2 EndY=-609.6 EndZ=0
    g4: GeomPoint X=0 Y=0 Z=0
  constraints (12):
    c: Coincident(g0,g1)
    c: Coincident(g1,g2)
    c: Coincident(g2,g3)
    c: Coincident(g3,g0)
    c: Horizontal(g1)
    c: Horizontal(g3)
    c: Vertical(g0)
    c: Vertical(g2)
    c: Symmetric(g1,g0,g4)
    c: Coincident(g4,g-1)
    c: DistanceX(g1,g1) = 2438.4
    c: DistanceY(g2,g2) = 1219.2
FEATURE [PartDesign::Pad] Pad034
  Direction = (0,0,1)
  Length = 19.05
  Length2 = 10
  Profile = -> Sketch042
  ReferenceAxis = -> Sketch042 [N_Axis]
  Type = 0
FEATURE [PartDesign::Body] Body032  label="B_Workbench_CutList_Plywood_Whole"
  Group = -> [Sketch042,Pad034]
  Origin = -> Origin055
  Tip = -> Pad034
PROVENANCE & LICENSES
A FreeCAD (.FCStd) document from a public repository crawl; recipes are the document's own serialized feature recipes (and, for linked parts, companion documents' recipes).
License: as declared in the source repository (recorded in the dataset sidecar).
